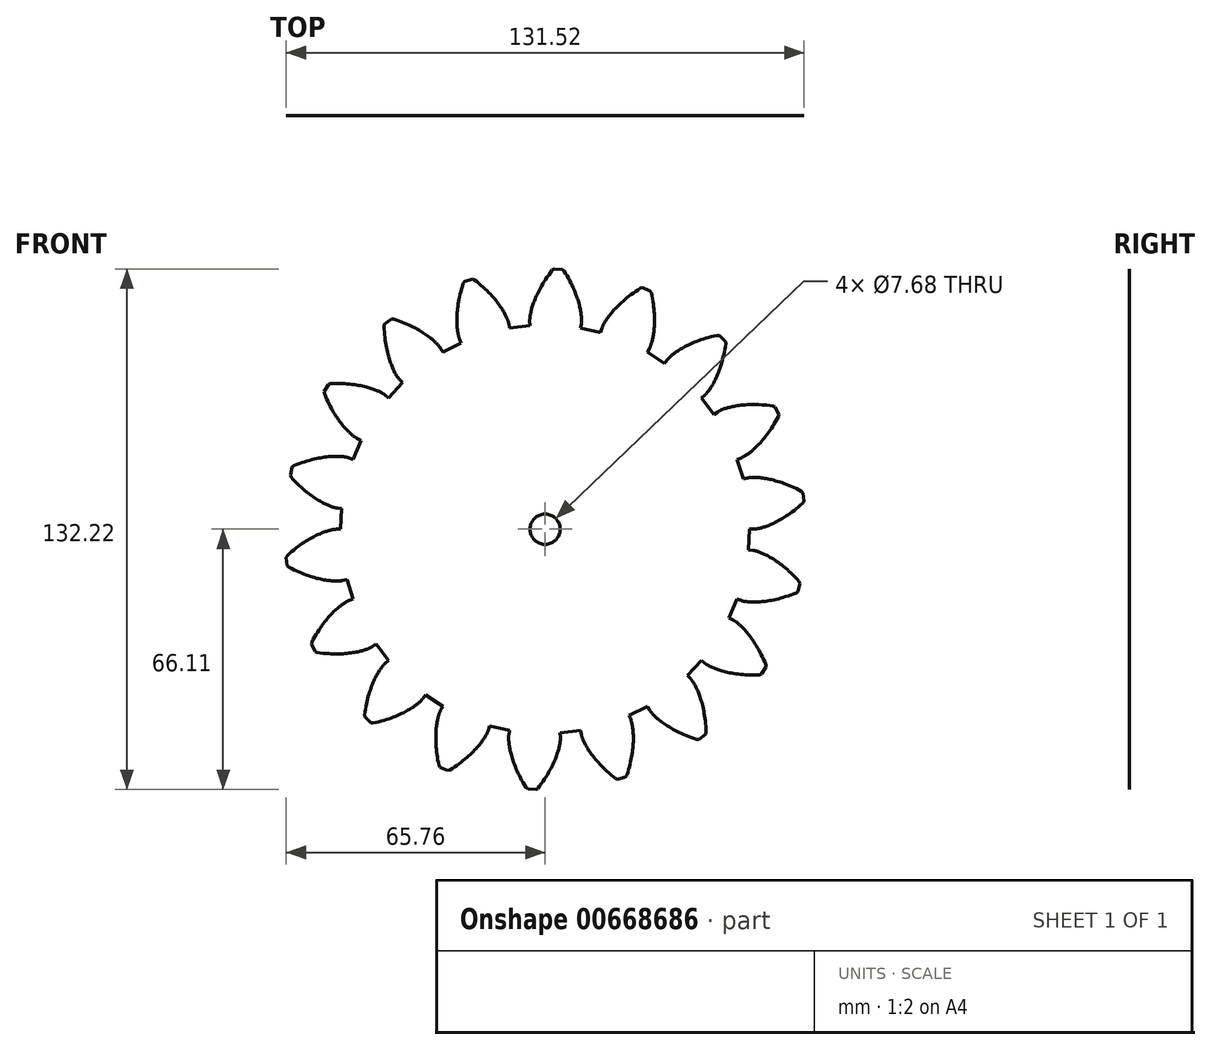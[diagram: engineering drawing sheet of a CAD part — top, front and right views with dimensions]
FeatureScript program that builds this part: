
annotation { "Feature Type Name" : "Feature", "Feature Type Description" : "" }
export const myFeature = defineFeature(function(context is Context, id is Id, definition is map)
    precondition{}
    {
        {
            var Q0;
            Q0=qCreatedBy(makeId("Front.planeOp"),FACE);
            var sketch = newSketch(context, id + "F0", { "sketchPlane" : qUnion([Q0])});
            skLineSegment(sketch, "E0", {"start": v(51.92, 0) * mm, "end": v(53.05, 0) * mm});
            skLineSegment(sketch, "E1", {"start": v(53.05, 0) * mm, "end": v(53.08, 0) * mm});
            skLineSegment(sketch, "E2", {"start": v(53.08, 0) * mm, "end": v(53.13, 0) * mm});
            skLineSegment(sketch, "E3", {"start": v(53.13, 0) * mm, "end": v(53.2, 0) * mm});
            skLineSegment(sketch, "E4", {"start": v(53.2, 0) * mm, "end": v(53.28, 0.01) * mm});
            skLineSegment(sketch, "E5", {"start": v(53.28, 0.01) * mm, "end": v(53.39, 0.03) * mm});
            skLineSegment(sketch, "E6", {"start": v(53.39, 0.03) * mm, "end": v(53.52, 0.04) * mm});
            skLineSegment(sketch, "E7", {"start": v(53.52, 0.04) * mm, "end": v(53.66, 0.06) * mm});
            skLineSegment(sketch, "E8", {"start": v(53.66, 0.06) * mm, "end": v(53.83, 0.1) * mm});
            skLineSegment(sketch, "E9", {"start": v(53.83, 0.1) * mm, "end": v(54.01, 0.12) * mm});
            skLineSegment(sketch, "E10", {"start": v(54.01, 0.12) * mm, "end": v(54.21, 0.17) * mm});
            skLineSegment(sketch, "E11", {"start": v(54.21, 0.17) * mm, "end": v(54.44, 0.22) * mm});
            skLineSegment(sketch, "E12", {"start": v(54.44, 0.22) * mm, "end": v(54.68, 0.28) * mm});
            skLineSegment(sketch, "E13", {"start": v(54.68, 0.28) * mm, "end": v(54.94, 0.34) * mm});
            skLineSegment(sketch, "E14", {"start": v(54.94, 0.34) * mm, "end": v(55.21, 0.42) * mm});
            skLineSegment(sketch, "E15", {"start": v(55.21, 0.42) * mm, "end": v(55.5, 0.51) * mm});
            skLineSegment(sketch, "E16", {"start": v(55.5, 0.51) * mm, "end": v(55.81, 0.62) * mm});
            skLineSegment(sketch, "E17", {"start": v(55.81, 0.62) * mm, "end": v(56.14, 0.73) * mm});
            skLineSegment(sketch, "E18", {"start": v(56.14, 0.73) * mm, "end": v(56.49, 0.86) * mm});
            skLineSegment(sketch, "E19", {"start": v(56.49, 0.86) * mm, "end": v(56.85, 1) * mm});
            skLineSegment(sketch, "E20", {"start": v(56.85, 1) * mm, "end": v(57.22, 1.16) * mm});
            skLineSegment(sketch, "E21", {"start": v(57.22, 1.16) * mm, "end": v(57.61, 1.33) * mm});
            skLineSegment(sketch, "E22", {"start": v(57.61, 1.33) * mm, "end": v(58.02, 1.52) * mm});
            skLineSegment(sketch, "E23", {"start": v(58.02, 1.52) * mm, "end": v(58.44, 1.72) * mm});
            skLineSegment(sketch, "E24", {"start": v(58.44, 1.72) * mm, "end": v(58.87, 1.94) * mm});
            skLineSegment(sketch, "E25", {"start": v(58.87, 1.94) * mm, "end": v(59.32, 2.18) * mm});
            skLineSegment(sketch, "E26", {"start": v(59.32, 2.18) * mm, "end": v(59.78, 2.44) * mm});
            skLineSegment(sketch, "E27", {"start": v(59.78, 2.44) * mm, "end": v(60.25, 2.72) * mm});
            skLineSegment(sketch, "E28", {"start": v(60.25, 2.72) * mm, "end": v(60.73, 3.01) * mm});
            skLineSegment(sketch, "E29", {"start": v(60.73, 3.01) * mm, "end": v(61.22, 3.33) * mm});
            skLineSegment(sketch, "E30", {"start": v(61.22, 3.33) * mm, "end": v(61.73, 3.67) * mm});
            skLineSegment(sketch, "E31", {"start": v(61.73, 3.67) * mm, "end": v(62.24, 4.03) * mm});
            skLineSegment(sketch, "E32", {"start": v(62.24, 4.03) * mm, "end": v(62.76, 4.4) * mm});
            skLineSegment(sketch, "E33", {"start": v(62.76, 4.4) * mm, "end": v(63.3, 4.8) * mm});
            skLineSegment(sketch, "E34", {"start": v(63.3, 4.8) * mm, "end": v(63.83, 5.23) * mm});
            skLineSegment(sketch, "E35", {"start": v(63.83, 5.23) * mm, "end": v(64.38, 5.68) * mm});
            skLineSegment(sketch, "E36", {"start": v(64.38, 5.68) * mm, "end": v(64.93, 6.15) * mm});
            skLineSegment(sketch, "E37", {"start": v(64.93, 6.15) * mm, "end": v(65.5, 6.65) * mm});
            skLineSegment(sketch, "E38", {"start": v(65.5, 6.65) * mm, "end": v(65.76, 7.14) * mm});
            skLineSegment(sketch, "E39", {"start": v(65.76, 7.14) * mm, "end": v(65.5, 9.23) * mm});
            skLineSegment(sketch, "E40", {"start": v(65.5, 9.23) * mm, "end": v(65.12, 9.64) * mm});
            skLineSegment(sketch, "E41", {"start": v(65.12, 9.64) * mm, "end": v(64.46, 9.98) * mm});
            skLineSegment(sketch, "E42", {"start": v(64.46, 9.98) * mm, "end": v(63.8, 10.3) * mm});
            skLineSegment(sketch, "E43", {"start": v(63.8, 10.3) * mm, "end": v(63.17, 10.6) * mm});
            skLineSegment(sketch, "E44", {"start": v(63.17, 10.6) * mm, "end": v(62.54, 10.88) * mm});
            skLineSegment(sketch, "E45", {"start": v(62.54, 10.88) * mm, "end": v(61.92, 11.14) * mm});
            skLineSegment(sketch, "E46", {"start": v(61.92, 11.14) * mm, "end": v(61.32, 11.38) * mm});
            skLineSegment(sketch, "E47", {"start": v(61.32, 11.38) * mm, "end": v(60.74, 11.6) * mm});
            skLineSegment(sketch, "E48", {"start": v(60.74, 11.6) * mm, "end": v(60.17, 11.8) * mm});
            skLineSegment(sketch, "E49", {"start": v(60.17, 11.8) * mm, "end": v(59.61, 12) * mm});
            skLineSegment(sketch, "E50", {"start": v(59.61, 12) * mm, "end": v(59.07, 12.16) * mm});
            skLineSegment(sketch, "E51", {"start": v(59.07, 12.16) * mm, "end": v(58.54, 12.31) * mm});
            skLineSegment(sketch, "E52", {"start": v(58.54, 12.31) * mm, "end": v(58.04, 12.45) * mm});
            skLineSegment(sketch, "E53", {"start": v(58.04, 12.45) * mm, "end": v(57.55, 12.57) * mm});
            skLineSegment(sketch, "E54", {"start": v(57.55, 12.57) * mm, "end": v(57.07, 12.68) * mm});
            skLineSegment(sketch, "E55", {"start": v(57.07, 12.68) * mm, "end": v(56.61, 12.78) * mm});
            skLineSegment(sketch, "E56", {"start": v(56.61, 12.78) * mm, "end": v(56.17, 12.86) * mm});
            skLineSegment(sketch, "E57", {"start": v(56.17, 12.86) * mm, "end": v(55.75, 12.93) * mm});
            skLineSegment(sketch, "E58", {"start": v(55.75, 12.93) * mm, "end": v(55.35, 13) * mm});
            skLineSegment(sketch, "E59", {"start": v(55.35, 13) * mm, "end": v(54.97, 13.04) * mm});
            skLineSegment(sketch, "E60", {"start": v(54.97, 13.04) * mm, "end": v(54.6, 13.08) * mm});
            skLineSegment(sketch, "E61", {"start": v(54.6, 13.08) * mm, "end": v(54.26, 13.11) * mm});
            skLineSegment(sketch, "E62", {"start": v(54.26, 13.11) * mm, "end": v(53.93, 13.13) * mm});
            skLineSegment(sketch, "E63", {"start": v(53.93, 13.13) * mm, "end": v(53.62, 13.15) * mm});
            skLineSegment(sketch, "E64", {"start": v(53.62, 13.15) * mm, "end": v(53.34, 13.16) * mm});
            skLineSegment(sketch, "E65", {"start": v(53.34, 13.16) * mm, "end": v(53.07, 13.16) * mm});
            skLineSegment(sketch, "E66", {"start": v(53.07, 13.16) * mm, "end": v(52.82, 13.16) * mm});
            skLineSegment(sketch, "E67", {"start": v(52.82, 13.16) * mm, "end": v(52.6, 13.15) * mm});
            skLineSegment(sketch, "E68", {"start": v(52.6, 13.15) * mm, "end": v(52.39, 13.15) * mm});
            skLineSegment(sketch, "E69", {"start": v(52.39, 13.15) * mm, "end": v(52.2, 13.13) * mm});
            skLineSegment(sketch, "E70", {"start": v(52.2, 13.13) * mm, "end": v(52.03, 13.12) * mm});
            skLineSegment(sketch, "E71", {"start": v(52.03, 13.12) * mm, "end": v(51.89, 13.1) * mm});
            skLineSegment(sketch, "E72", {"start": v(51.89, 13.1) * mm, "end": v(51.76, 13.09) * mm});
            skLineSegment(sketch, "E73", {"start": v(51.76, 13.09) * mm, "end": v(51.65, 13.07) * mm});
            skLineSegment(sketch, "E74", {"start": v(51.65, 13.07) * mm, "end": v(51.57, 13.06) * mm});
            skLineSegment(sketch, "E75", {"start": v(51.57, 13.06) * mm, "end": v(51.5, 13.05) * mm});
            skLineSegment(sketch, "E76", {"start": v(51.5, 13.05) * mm, "end": v(51.45, 13.04) * mm});
            skLineSegment(sketch, "E77", {"start": v(51.45, 13.04) * mm, "end": v(51.43, 13.03) * mm});
            skLineSegment(sketch, "E78", {"start": v(51.43, 13.03) * mm, "end": v(50.33, 12.75) * mm});
            skLineSegment(sketch, "E79", {"start": v(50.33, 12.75) * mm, "end": v(48.8, 17.76) * mm});
            skLineSegment(sketch, "E80", {"start": v(48.8, 17.76) * mm, "end": v(49.85, 18.14) * mm});
            skLineSegment(sketch, "E81", {"start": v(49.85, 18.14) * mm, "end": v(49.88, 18.15) * mm});
            skLineSegment(sketch, "E82", {"start": v(49.88, 18.15) * mm, "end": v(49.92, 18.17) * mm});
            skLineSegment(sketch, "E83", {"start": v(49.92, 18.17) * mm, "end": v(49.98, 18.2) * mm});
            skLineSegment(sketch, "E84", {"start": v(49.98, 18.2) * mm, "end": v(50.06, 18.24) * mm});
            skLineSegment(sketch, "E85", {"start": v(50.06, 18.24) * mm, "end": v(50.16, 18.29) * mm});
            skLineSegment(sketch, "E86", {"start": v(50.16, 18.29) * mm, "end": v(50.27, 18.34) * mm});
            skLineSegment(sketch, "E87", {"start": v(50.27, 18.34) * mm, "end": v(50.4, 18.41) * mm});
            skLineSegment(sketch, "E88", {"start": v(50.4, 18.41) * mm, "end": v(50.55, 18.5) * mm});
            skLineSegment(sketch, "E89", {"start": v(50.55, 18.5) * mm, "end": v(50.71, 18.59) * mm});
            skLineSegment(sketch, "E90", {"start": v(50.71, 18.59) * mm, "end": v(50.89, 18.7) * mm});
            skLineSegment(sketch, "E91", {"start": v(50.89, 18.7) * mm, "end": v(51.08, 18.82) * mm});
            skLineSegment(sketch, "E92", {"start": v(51.08, 18.82) * mm, "end": v(51.29, 18.96) * mm});
            skLineSegment(sketch, "E93", {"start": v(51.29, 18.96) * mm, "end": v(51.5, 19.11) * mm});
            skLineSegment(sketch, "E94", {"start": v(51.5, 19.11) * mm, "end": v(51.74, 19.28) * mm});
            skLineSegment(sketch, "E95", {"start": v(51.74, 19.28) * mm, "end": v(51.98, 19.47) * mm});
            skLineSegment(sketch, "E96", {"start": v(51.98, 19.47) * mm, "end": v(52.24, 19.67) * mm});
            skLineSegment(sketch, "E97", {"start": v(52.24, 19.67) * mm, "end": v(52.5, 19.89) * mm});
            skLineSegment(sketch, "E98", {"start": v(52.5, 19.89) * mm, "end": v(52.79, 20.13) * mm});
            skLineSegment(sketch, "E99", {"start": v(52.79, 20.13) * mm, "end": v(53.08, 20.38) * mm});
            skLineSegment(sketch, "E100", {"start": v(53.08, 20.38) * mm, "end": v(53.38, 20.66) * mm});
            skLineSegment(sketch, "E101", {"start": v(53.38, 20.66) * mm, "end": v(53.68, 20.95) * mm});
            skLineSegment(sketch, "E102", {"start": v(53.68, 20.95) * mm, "end": v(54, 21.27) * mm});
            skLineSegment(sketch, "E103", {"start": v(54, 21.27) * mm, "end": v(54.32, 21.6) * mm});
            skLineSegment(sketch, "E104", {"start": v(54.32, 21.6) * mm, "end": v(54.66, 21.96) * mm});
            skLineSegment(sketch, "E105", {"start": v(54.66, 21.96) * mm, "end": v(55, 22.34) * mm});
            skLineSegment(sketch, "E106", {"start": v(55, 22.34) * mm, "end": v(55.34, 22.74) * mm});
            skLineSegment(sketch, "E107", {"start": v(55.34, 22.74) * mm, "end": v(55.68, 23.16) * mm});
            skLineSegment(sketch, "E108", {"start": v(55.68, 23.16) * mm, "end": v(56.04, 23.6) * mm});
            skLineSegment(sketch, "E109", {"start": v(56.04, 23.6) * mm, "end": v(56.4, 24.07) * mm});
            skLineSegment(sketch, "E110", {"start": v(56.4, 24.07) * mm, "end": v(56.75, 24.56) * mm});
            skLineSegment(sketch, "E111", {"start": v(56.75, 24.56) * mm, "end": v(57.11, 25.07) * mm});
            skLineSegment(sketch, "E112", {"start": v(57.11, 25.07) * mm, "end": v(57.47, 25.6) * mm});
            skLineSegment(sketch, "E113", {"start": v(57.47, 25.6) * mm, "end": v(57.83, 26.17) * mm});
            skLineSegment(sketch, "E114", {"start": v(57.83, 26.17) * mm, "end": v(58.2, 26.75) * mm});
            skLineSegment(sketch, "E115", {"start": v(58.2, 26.75) * mm, "end": v(58.56, 27.36) * mm});
            skLineSegment(sketch, "E116", {"start": v(58.56, 27.36) * mm, "end": v(58.91, 28) * mm});
            skLineSegment(sketch, "E117", {"start": v(58.91, 28) * mm, "end": v(59.27, 28.65) * mm});
            skLineSegment(sketch, "E118", {"start": v(59.27, 28.65) * mm, "end": v(59.35, 29.2) * mm});
            skLineSegment(sketch, "E119", {"start": v(59.35, 29.2) * mm, "end": v(58.39, 31.08) * mm});
            skLineSegment(sketch, "E120", {"start": v(58.39, 31.08) * mm, "end": v(57.9, 31.33) * mm});
            skLineSegment(sketch, "E121", {"start": v(57.9, 31.33) * mm, "end": v(57.15, 31.43) * mm});
            skLineSegment(sketch, "E122", {"start": v(57.15, 31.43) * mm, "end": v(56.43, 31.5) * mm});
            skLineSegment(sketch, "E123", {"start": v(56.43, 31.5) * mm, "end": v(55.73, 31.57) * mm});
            skLineSegment(sketch, "E124", {"start": v(55.73, 31.57) * mm, "end": v(55.04, 31.62) * mm});
            skLineSegment(sketch, "E125", {"start": v(55.04, 31.62) * mm, "end": v(54.38, 31.65) * mm});
            skLineSegment(sketch, "E126", {"start": v(54.38, 31.65) * mm, "end": v(53.73, 31.67) * mm});
            skLineSegment(sketch, "E127", {"start": v(53.73, 31.67) * mm, "end": v(53.1, 31.68) * mm});
            skLineSegment(sketch, "E128", {"start": v(53.1, 31.68) * mm, "end": v(52.5, 31.67) * mm});
            skLineSegment(sketch, "E129", {"start": v(52.5, 31.67) * mm, "end": v(51.91, 31.66) * mm});
            skLineSegment(sketch, "E130", {"start": v(51.91, 31.66) * mm, "end": v(51.35, 31.63) * mm});
            skLineSegment(sketch, "E131", {"start": v(51.35, 31.63) * mm, "end": v(50.8, 31.6) * mm});
            skLineSegment(sketch, "E132", {"start": v(50.8, 31.6) * mm, "end": v(50.28, 31.55) * mm});
            skLineSegment(sketch, "E133", {"start": v(50.28, 31.55) * mm, "end": v(49.77, 31.5) * mm});
            skLineSegment(sketch, "E134", {"start": v(49.77, 31.5) * mm, "end": v(49.3, 31.44) * mm});
            skLineSegment(sketch, "E135", {"start": v(49.3, 31.44) * mm, "end": v(48.83, 31.37) * mm});
            skLineSegment(sketch, "E136", {"start": v(48.83, 31.37) * mm, "end": v(48.39, 31.3) * mm});
            skLineSegment(sketch, "E137", {"start": v(48.39, 31.3) * mm, "end": v(47.97, 31.22) * mm});
            skLineSegment(sketch, "E138", {"start": v(47.97, 31.22) * mm, "end": v(47.57, 31.14) * mm});
            skLineSegment(sketch, "E139", {"start": v(47.57, 31.14) * mm, "end": v(47.2, 31.05) * mm});
            skLineSegment(sketch, "E140", {"start": v(47.2, 31.05) * mm, "end": v(46.84, 30.97) * mm});
            skLineSegment(sketch, "E141", {"start": v(46.84, 30.97) * mm, "end": v(46.5, 30.88) * mm});
            skLineSegment(sketch, "E142", {"start": v(46.5, 30.88) * mm, "end": v(46.19, 30.79) * mm});
            skLineSegment(sketch, "E143", {"start": v(46.19, 30.79) * mm, "end": v(45.9, 30.7) * mm});
            skLineSegment(sketch, "E144", {"start": v(45.9, 30.7) * mm, "end": v(45.62, 30.6) * mm});
            skLineSegment(sketch, "E145", {"start": v(45.62, 30.6) * mm, "end": v(45.37, 30.52) * mm});
            skLineSegment(sketch, "E146", {"start": v(45.37, 30.52) * mm, "end": v(45.13, 30.43) * mm});
            skLineSegment(sketch, "E147", {"start": v(45.13, 30.43) * mm, "end": v(44.92, 30.35) * mm});
            skLineSegment(sketch, "E148", {"start": v(44.92, 30.35) * mm, "end": v(44.73, 30.27) * mm});
            skLineSegment(sketch, "E149", {"start": v(44.73, 30.27) * mm, "end": v(44.56, 30.2) * mm});
            skLineSegment(sketch, "E150", {"start": v(44.56, 30.2) * mm, "end": v(44.4, 30.12) * mm});
            skLineSegment(sketch, "E151", {"start": v(44.4, 30.12) * mm, "end": v(44.28, 30.06) * mm});
            skLineSegment(sketch, "E152", {"start": v(44.28, 30.06) * mm, "end": v(44.16, 30) * mm});
            skLineSegment(sketch, "E153", {"start": v(44.16, 30) * mm, "end": v(44.07, 29.95) * mm});
            skLineSegment(sketch, "E154", {"start": v(44.07, 29.95) * mm, "end": v(44, 29.9) * mm});
            skLineSegment(sketch, "E155", {"start": v(44, 29.9) * mm, "end": v(43.93, 29.87) * mm});
            skLineSegment(sketch, "E156", {"start": v(43.93, 29.87) * mm, "end": v(43.9, 29.85) * mm});
            skLineSegment(sketch, "E157", {"start": v(43.9, 29.85) * mm, "end": v(43.87, 29.83) * mm});
            skLineSegment(sketch, "E158", {"start": v(43.87, 29.83) * mm, "end": v(42.94, 29.2) * mm});
            skLineSegment(sketch, "E159", {"start": v(42.94, 29.2) * mm, "end": v(39.78, 33.38) * mm});
            skLineSegment(sketch, "E160", {"start": v(39.78, 33.38) * mm, "end": v(40.64, 34.1) * mm});
            skLineSegment(sketch, "E161", {"start": v(40.64, 34.1) * mm, "end": v(40.66, 34.12) * mm});
            skLineSegment(sketch, "E162", {"start": v(40.66, 34.12) * mm, "end": v(40.7, 34.15) * mm});
            skLineSegment(sketch, "E163", {"start": v(40.7, 34.15) * mm, "end": v(40.74, 34.2) * mm});
            skLineSegment(sketch, "E164", {"start": v(40.74, 34.2) * mm, "end": v(40.8, 34.26) * mm});
            skLineSegment(sketch, "E165", {"start": v(40.8, 34.26) * mm, "end": v(40.88, 34.34) * mm});
            skLineSegment(sketch, "E166", {"start": v(40.88, 34.34) * mm, "end": v(40.97, 34.43) * mm});
            skLineSegment(sketch, "E167", {"start": v(40.97, 34.43) * mm, "end": v(41.07, 34.54) * mm});
            skLineSegment(sketch, "E168", {"start": v(41.07, 34.54) * mm, "end": v(41.18, 34.67) * mm});
            skLineSegment(sketch, "E169", {"start": v(41.18, 34.67) * mm, "end": v(41.3, 34.81) * mm});
            skLineSegment(sketch, "E170", {"start": v(41.3, 34.81) * mm, "end": v(41.42, 34.98) * mm});
            skLineSegment(sketch, "E171", {"start": v(41.42, 34.98) * mm, "end": v(41.56, 35.16) * mm});
            skLineSegment(sketch, "E172", {"start": v(41.56, 35.16) * mm, "end": v(41.7, 35.36) * mm});
            skLineSegment(sketch, "E173", {"start": v(41.7, 35.36) * mm, "end": v(41.86, 35.58) * mm});
            skLineSegment(sketch, "E174", {"start": v(41.86, 35.58) * mm, "end": v(42.02, 35.81) * mm});
            skLineSegment(sketch, "E175", {"start": v(42.02, 35.81) * mm, "end": v(42.19, 36.07) * mm});
            skLineSegment(sketch, "E176", {"start": v(42.19, 36.07) * mm, "end": v(42.36, 36.35) * mm});
            skLineSegment(sketch, "E177", {"start": v(42.36, 36.35) * mm, "end": v(42.54, 36.65) * mm});
            skLineSegment(sketch, "E178", {"start": v(42.54, 36.65) * mm, "end": v(42.72, 36.97) * mm});
            skLineSegment(sketch, "E179", {"start": v(42.72, 36.97) * mm, "end": v(42.9, 37.3) * mm});
            skLineSegment(sketch, "E180", {"start": v(42.9, 37.3) * mm, "end": v(43.09, 37.67) * mm});
            skLineSegment(sketch, "E181", {"start": v(43.09, 37.67) * mm, "end": v(43.28, 38.05) * mm});
            skLineSegment(sketch, "E182", {"start": v(43.28, 38.05) * mm, "end": v(43.47, 38.46) * mm});
            skLineSegment(sketch, "E183", {"start": v(43.47, 38.46) * mm, "end": v(43.66, 38.88) * mm});
            skLineSegment(sketch, "E184", {"start": v(43.66, 38.88) * mm, "end": v(43.85, 39.33) * mm});
            skLineSegment(sketch, "E185", {"start": v(43.85, 39.33) * mm, "end": v(44.04, 39.8) * mm});
            skLineSegment(sketch, "E186", {"start": v(44.04, 39.8) * mm, "end": v(44.22, 40.3) * mm});
            skLineSegment(sketch, "E187", {"start": v(44.22, 40.3) * mm, "end": v(44.4, 40.8) * mm});
            skLineSegment(sketch, "E188", {"start": v(44.4, 40.8) * mm, "end": v(44.58, 41.35) * mm});
            skLineSegment(sketch, "E189", {"start": v(44.58, 41.35) * mm, "end": v(44.76, 41.9) * mm});
            skLineSegment(sketch, "E190", {"start": v(44.76, 41.9) * mm, "end": v(44.93, 42.49) * mm});
            skLineSegment(sketch, "E191", {"start": v(44.93, 42.49) * mm, "end": v(45.1, 43.1) * mm});
            skLineSegment(sketch, "E192", {"start": v(45.1, 43.1) * mm, "end": v(45.25, 43.72) * mm});
            skLineSegment(sketch, "E193", {"start": v(45.25, 43.72) * mm, "end": v(45.4, 44.37) * mm});
            skLineSegment(sketch, "E194", {"start": v(45.4, 44.37) * mm, "end": v(45.54, 45.04) * mm});
            skLineSegment(sketch, "E195", {"start": v(45.54, 45.04) * mm, "end": v(45.67, 45.74) * mm});
            skLineSegment(sketch, "E196", {"start": v(45.67, 45.74) * mm, "end": v(45.79, 46.45) * mm});
            skLineSegment(sketch, "E197", {"start": v(45.79, 46.45) * mm, "end": v(45.9, 47.19) * mm});
            skLineSegment(sketch, "E198", {"start": v(45.9, 47.19) * mm, "end": v(45.79, 47.74) * mm});
            skLineSegment(sketch, "E199", {"start": v(45.79, 47.74) * mm, "end": v(44.24, 49.18) * mm});
            skLineSegment(sketch, "E200", {"start": v(44.24, 49.18) * mm, "end": v(43.69, 49.24) * mm});
            skLineSegment(sketch, "E201", {"start": v(43.69, 49.24) * mm, "end": v(42.96, 49.08) * mm});
            skLineSegment(sketch, "E202", {"start": v(42.96, 49.08) * mm, "end": v(42.25, 48.9) * mm});
            skLineSegment(sketch, "E203", {"start": v(42.25, 48.9) * mm, "end": v(41.57, 48.72) * mm});
            skLineSegment(sketch, "E204", {"start": v(41.57, 48.72) * mm, "end": v(40.91, 48.54) * mm});
            skLineSegment(sketch, "E205", {"start": v(40.91, 48.54) * mm, "end": v(40.27, 48.34) * mm});
            skLineSegment(sketch, "E206", {"start": v(40.27, 48.34) * mm, "end": v(39.66, 48.14) * mm});
            skLineSegment(sketch, "E207", {"start": v(39.66, 48.14) * mm, "end": v(39.07, 47.93) * mm});
            skLineSegment(sketch, "E208", {"start": v(39.07, 47.93) * mm, "end": v(38.5, 47.72) * mm});
            skLineSegment(sketch, "E209", {"start": v(38.5, 47.72) * mm, "end": v(37.96, 47.5) * mm});
            skLineSegment(sketch, "E210", {"start": v(37.96, 47.5) * mm, "end": v(37.43, 47.29) * mm});
            skLineSegment(sketch, "E211", {"start": v(37.43, 47.29) * mm, "end": v(36.93, 47.07) * mm});
            skLineSegment(sketch, "E212", {"start": v(36.93, 47.07) * mm, "end": v(36.45, 46.84) * mm});
            skLineSegment(sketch, "E213", {"start": v(36.45, 46.84) * mm, "end": v(36, 46.62) * mm});
            skLineSegment(sketch, "E214", {"start": v(36, 46.62) * mm, "end": v(35.57, 46.4) * mm});
            skLineSegment(sketch, "E215", {"start": v(35.57, 46.4) * mm, "end": v(35.15, 46.18) * mm});
            skLineSegment(sketch, "E216", {"start": v(35.15, 46.18) * mm, "end": v(34.77, 45.96) * mm});
            skLineSegment(sketch, "E217", {"start": v(34.77, 45.96) * mm, "end": v(34.4, 45.74) * mm});
            skLineSegment(sketch, "E218", {"start": v(34.4, 45.74) * mm, "end": v(34.05, 45.53) * mm});
            skLineSegment(sketch, "E219", {"start": v(34.05, 45.53) * mm, "end": v(33.72, 45.32) * mm});
            skLineSegment(sketch, "E220", {"start": v(33.72, 45.32) * mm, "end": v(33.42, 45.12) * mm});
            skLineSegment(sketch, "E221", {"start": v(33.42, 45.12) * mm, "end": v(33.13, 44.92) * mm});
            skLineSegment(sketch, "E222", {"start": v(33.13, 44.92) * mm, "end": v(32.87, 44.73) * mm});
            skLineSegment(sketch, "E223", {"start": v(32.87, 44.73) * mm, "end": v(32.62, 44.54) * mm});
            skLineSegment(sketch, "E224", {"start": v(32.62, 44.54) * mm, "end": v(32.4, 44.36) * mm});
            skLineSegment(sketch, "E225", {"start": v(32.4, 44.36) * mm, "end": v(32.2, 44.2) * mm});
            skLineSegment(sketch, "E226", {"start": v(32.2, 44.2) * mm, "end": v(32, 44.03) * mm});
            skLineSegment(sketch, "E227", {"start": v(32, 44.03) * mm, "end": v(31.83, 43.88) * mm});
            skLineSegment(sketch, "E228", {"start": v(31.83, 43.88) * mm, "end": v(31.68, 43.74) * mm});
            skLineSegment(sketch, "E229", {"start": v(31.68, 43.74) * mm, "end": v(31.55, 43.61) * mm});
            skLineSegment(sketch, "E230", {"start": v(31.55, 43.61) * mm, "end": v(31.43, 43.5) * mm});
            skLineSegment(sketch, "E231", {"start": v(31.43, 43.5) * mm, "end": v(31.33, 43.39) * mm});
            skLineSegment(sketch, "E232", {"start": v(31.33, 43.39) * mm, "end": v(31.24, 43.3) * mm});
            skLineSegment(sketch, "E233", {"start": v(31.24, 43.3) * mm, "end": v(31.17, 43.22) * mm});
            skLineSegment(sketch, "E234", {"start": v(31.17, 43.22) * mm, "end": v(31.1, 43.15) * mm});
            skLineSegment(sketch, "E235", {"start": v(31.1, 43.15) * mm, "end": v(31.07, 43.1) * mm});
            skLineSegment(sketch, "E236", {"start": v(31.07, 43.1) * mm, "end": v(31.04, 43.06) * mm});
            skLineSegment(sketch, "E237", {"start": v(31.04, 43.06) * mm, "end": v(31.02, 43.04) * mm});
            skLineSegment(sketch, "E238", {"start": v(31.02, 43.04) * mm, "end": v(30.36, 42.12) * mm});
            skLineSegment(sketch, "E239", {"start": v(30.36, 42.12) * mm, "end": v(25.96, 44.97) * mm});
            skLineSegment(sketch, "E240", {"start": v(25.96, 44.97) * mm, "end": v(26.53, 45.94) * mm});
            skLineSegment(sketch, "E241", {"start": v(26.53, 45.94) * mm, "end": v(26.54, 45.97) * mm});
            skLineSegment(sketch, "E242", {"start": v(26.54, 45.97) * mm, "end": v(26.56, 46) * mm});
            skLineSegment(sketch, "E243", {"start": v(26.56, 46) * mm, "end": v(26.6, 46.07) * mm});
            skLineSegment(sketch, "E244", {"start": v(26.6, 46.07) * mm, "end": v(26.63, 46.15) * mm});
            skLineSegment(sketch, "E245", {"start": v(26.63, 46.15) * mm, "end": v(26.67, 46.25) * mm});
            skLineSegment(sketch, "E246", {"start": v(26.67, 46.25) * mm, "end": v(26.72, 46.37) * mm});
            skLineSegment(sketch, "E247", {"start": v(26.72, 46.37) * mm, "end": v(26.78, 46.5) * mm});
            skLineSegment(sketch, "E248", {"start": v(26.78, 46.5) * mm, "end": v(26.83, 46.66) * mm});
            skLineSegment(sketch, "E249", {"start": v(26.83, 46.66) * mm, "end": v(26.9, 46.84) * mm});
            skLineSegment(sketch, "E250", {"start": v(26.9, 46.84) * mm, "end": v(26.96, 47.03) * mm});
            skLineSegment(sketch, "E251", {"start": v(26.96, 47.03) * mm, "end": v(27.03, 47.25) * mm});
            skLineSegment(sketch, "E252", {"start": v(27.03, 47.25) * mm, "end": v(27.1, 47.49) * mm});
            skLineSegment(sketch, "E253", {"start": v(27.1, 47.49) * mm, "end": v(27.17, 47.75) * mm});
            skLineSegment(sketch, "E254", {"start": v(27.17, 47.75) * mm, "end": v(27.24, 48.03) * mm});
            skLineSegment(sketch, "E255", {"start": v(27.24, 48.03) * mm, "end": v(27.3, 48.32) * mm});
            skLineSegment(sketch, "E256", {"start": v(27.3, 48.32) * mm, "end": v(27.37, 48.64) * mm});
            skLineSegment(sketch, "E257", {"start": v(27.37, 48.64) * mm, "end": v(27.44, 48.99) * mm});
            skLineSegment(sketch, "E258", {"start": v(27.44, 48.99) * mm, "end": v(27.5, 49.35) * mm});
            skLineSegment(sketch, "E259", {"start": v(27.5, 49.35) * mm, "end": v(27.56, 49.73) * mm});
            skLineSegment(sketch, "E260", {"start": v(27.56, 49.73) * mm, "end": v(27.6, 50.13) * mm});
            skLineSegment(sketch, "E261", {"start": v(27.6, 50.13) * mm, "end": v(27.65, 50.56) * mm});
            skLineSegment(sketch, "E262", {"start": v(27.65, 50.56) * mm, "end": v(27.7, 51) * mm});
            skLineSegment(sketch, "E263", {"start": v(27.7, 51) * mm, "end": v(27.73, 51.47) * mm});
            skLineSegment(sketch, "E264", {"start": v(27.73, 51.47) * mm, "end": v(27.75, 51.96) * mm});
            skLineSegment(sketch, "E265", {"start": v(27.75, 51.96) * mm, "end": v(27.77, 52.46) * mm});
            skLineSegment(sketch, "E266", {"start": v(27.77, 52.46) * mm, "end": v(27.77, 52.99) * mm});
            skLineSegment(sketch, "E267", {"start": v(27.77, 52.99) * mm, "end": v(27.77, 53.54) * mm});
            skLineSegment(sketch, "E268", {"start": v(27.77, 53.54) * mm, "end": v(27.75, 54.1) * mm});
            skLineSegment(sketch, "E269", {"start": v(27.75, 54.1) * mm, "end": v(27.73, 54.69) * mm});
            skLineSegment(sketch, "E270", {"start": v(27.73, 54.69) * mm, "end": v(27.69, 55.3) * mm});
            skLineSegment(sketch, "E271", {"start": v(27.69, 55.3) * mm, "end": v(27.63, 55.92) * mm});
            skLineSegment(sketch, "E272", {"start": v(27.63, 55.92) * mm, "end": v(27.56, 56.56) * mm});
            skLineSegment(sketch, "E273", {"start": v(27.56, 56.56) * mm, "end": v(27.48, 57.22) * mm});
            skLineSegment(sketch, "E274", {"start": v(27.48, 57.22) * mm, "end": v(27.38, 57.9) * mm});
            skLineSegment(sketch, "E275", {"start": v(27.38, 57.9) * mm, "end": v(27.27, 58.6) * mm});
            skLineSegment(sketch, "E276", {"start": v(27.27, 58.6) * mm, "end": v(27.14, 59.31) * mm});
            skLineSegment(sketch, "E277", {"start": v(27.14, 59.31) * mm, "end": v(26.99, 60.04) * mm});
            skLineSegment(sketch, "E278", {"start": v(26.99, 60.04) * mm, "end": v(26.7, 60.52) * mm});
            skLineSegment(sketch, "E279", {"start": v(26.7, 60.52) * mm, "end": v(24.75, 61.34) * mm});
            skLineSegment(sketch, "E280", {"start": v(24.75, 61.34) * mm, "end": v(24.2, 61.22) * mm});
            skLineSegment(sketch, "E281", {"start": v(24.2, 61.22) * mm, "end": v(23.58, 60.81) * mm});
            skLineSegment(sketch, "E282", {"start": v(23.58, 60.81) * mm, "end": v(22.98, 60.4) * mm});
            skLineSegment(sketch, "E283", {"start": v(22.98, 60.4) * mm, "end": v(22.4, 60) * mm});
            skLineSegment(sketch, "E284", {"start": v(22.4, 60) * mm, "end": v(21.84, 59.6) * mm});
            skLineSegment(sketch, "E285", {"start": v(21.84, 59.6) * mm, "end": v(21.31, 59.2) * mm});
            skLineSegment(sketch, "E286", {"start": v(21.31, 59.2) * mm, "end": v(20.8, 58.8) * mm});
            skLineSegment(sketch, "E287", {"start": v(20.8, 58.8) * mm, "end": v(20.32, 58.4) * mm});
            skLineSegment(sketch, "E288", {"start": v(20.32, 58.4) * mm, "end": v(19.86, 58.01) * mm});
            skLineSegment(sketch, "E289", {"start": v(19.86, 58.01) * mm, "end": v(19.42, 57.62) * mm});
            skLineSegment(sketch, "E290", {"start": v(19.42, 57.62) * mm, "end": v(19, 57.24) * mm});
            skLineSegment(sketch, "E291", {"start": v(19, 57.24) * mm, "end": v(18.6, 56.86) * mm});
            skLineSegment(sketch, "E292", {"start": v(18.6, 56.86) * mm, "end": v(18.24, 56.49) * mm});
            skLineSegment(sketch, "E293", {"start": v(18.24, 56.49) * mm, "end": v(17.88, 56.12) * mm});
            skLineSegment(sketch, "E294", {"start": v(17.88, 56.12) * mm, "end": v(17.55, 55.77) * mm});
            skLineSegment(sketch, "E295", {"start": v(17.55, 55.77) * mm, "end": v(17.24, 55.42) * mm});
            skLineSegment(sketch, "E296", {"start": v(17.24, 55.42) * mm, "end": v(16.95, 55.08) * mm});
            skLineSegment(sketch, "E297", {"start": v(16.95, 55.08) * mm, "end": v(16.68, 54.75) * mm});
            skLineSegment(sketch, "E298", {"start": v(16.68, 54.75) * mm, "end": v(16.43, 54.43) * mm});
            skLineSegment(sketch, "E299", {"start": v(16.43, 54.43) * mm, "end": v(16.19, 54.12) * mm});
            skLineSegment(sketch, "E300", {"start": v(16.19, 54.12) * mm, "end": v(15.97, 53.83) * mm});
            skLineSegment(sketch, "E301", {"start": v(15.97, 53.83) * mm, "end": v(15.77, 53.54) * mm});
            skLineSegment(sketch, "E302", {"start": v(15.77, 53.54) * mm, "end": v(15.59, 53.27) * mm});
            skLineSegment(sketch, "E303", {"start": v(15.59, 53.27) * mm, "end": v(15.42, 53.01) * mm});
            skLineSegment(sketch, "E304", {"start": v(15.42, 53.01) * mm, "end": v(15.27, 52.77) * mm});
            skLineSegment(sketch, "E305", {"start": v(15.27, 52.77) * mm, "end": v(15.14, 52.54) * mm});
            skLineSegment(sketch, "E306", {"start": v(15.14, 52.54) * mm, "end": v(15.01, 52.33) * mm});
            skLineSegment(sketch, "E307", {"start": v(15.01, 52.33) * mm, "end": v(14.9, 52.13) * mm});
            skLineSegment(sketch, "E308", {"start": v(14.9, 52.13) * mm, "end": v(14.8, 51.94) * mm});
            skLineSegment(sketch, "E309", {"start": v(14.8, 51.94) * mm, "end": v(14.73, 51.77) * mm});
            skLineSegment(sketch, "E310", {"start": v(14.73, 51.77) * mm, "end": v(14.66, 51.62) * mm});
            skLineSegment(sketch, "E311", {"start": v(14.66, 51.62) * mm, "end": v(14.6, 51.49) * mm});
            skLineSegment(sketch, "E312", {"start": v(14.6, 51.49) * mm, "end": v(14.55, 51.37) * mm});
            skLineSegment(sketch, "E313", {"start": v(14.55, 51.37) * mm, "end": v(14.5, 51.27) * mm});
            skLineSegment(sketch, "E314", {"start": v(14.5, 51.27) * mm, "end": v(14.47, 51.19) * mm});
            skLineSegment(sketch, "E315", {"start": v(14.47, 51.19) * mm, "end": v(14.45, 51.12) * mm});
            skLineSegment(sketch, "E316", {"start": v(14.45, 51.12) * mm, "end": v(14.44, 51.08) * mm});
            skLineSegment(sketch, "E317", {"start": v(14.44, 51.08) * mm, "end": v(14.43, 51.05) * mm});
            skLineSegment(sketch, "E318", {"start": v(14.43, 51.05) * mm, "end": v(14.12, 49.97) * mm});
            skLineSegment(sketch, "E319", {"start": v(14.12, 49.97) * mm, "end": v(9.02, 51.14) * mm});
            skLineSegment(sketch, "E320", {"start": v(9.02, 51.14) * mm, "end": v(9.21, 52.24) * mm});
            skLineSegment(sketch, "E321", {"start": v(9.21, 52.24) * mm, "end": v(9.22, 52.27) * mm});
            skLineSegment(sketch, "E322", {"start": v(9.22, 52.27) * mm, "end": v(9.22, 52.32) * mm});
            skLineSegment(sketch, "E323", {"start": v(9.22, 52.32) * mm, "end": v(9.23, 52.39) * mm});
            skLineSegment(sketch, "E324", {"start": v(9.23, 52.39) * mm, "end": v(9.24, 52.47) * mm});
            skLineSegment(sketch, "E325", {"start": v(9.24, 52.47) * mm, "end": v(9.25, 52.58) * mm});
            skLineSegment(sketch, "E326", {"start": v(9.25, 52.58) * mm, "end": v(9.25, 52.7) * mm});
            skLineSegment(sketch, "E327", {"start": v(9.25, 52.7) * mm, "end": v(9.26, 52.86) * mm});
            skLineSegment(sketch, "E328", {"start": v(9.26, 52.86) * mm, "end": v(9.26, 53.03) * mm});
            skLineSegment(sketch, "E329", {"start": v(9.26, 53.03) * mm, "end": v(9.26, 53.21) * mm});
            skLineSegment(sketch, "E330", {"start": v(9.26, 53.21) * mm, "end": v(9.25, 53.42) * mm});
            skLineSegment(sketch, "E331", {"start": v(9.25, 53.42) * mm, "end": v(9.24, 53.65) * mm});
            skLineSegment(sketch, "E332", {"start": v(9.24, 53.65) * mm, "end": v(9.22, 53.9) * mm});
            skLineSegment(sketch, "E333", {"start": v(9.22, 53.9) * mm, "end": v(9.2, 54.16) * mm});
            skLineSegment(sketch, "E334", {"start": v(9.2, 54.16) * mm, "end": v(9.17, 54.45) * mm});
            skLineSegment(sketch, "E335", {"start": v(9.17, 54.45) * mm, "end": v(9.13, 54.75) * mm});
            skLineSegment(sketch, "E336", {"start": v(9.13, 54.75) * mm, "end": v(9.09, 55.07) * mm});
            skLineSegment(sketch, "E337", {"start": v(9.09, 55.07) * mm, "end": v(9.03, 55.42) * mm});
            skLineSegment(sketch, "E338", {"start": v(9.03, 55.42) * mm, "end": v(8.96, 55.78) * mm});
            skLineSegment(sketch, "E339", {"start": v(8.96, 55.78) * mm, "end": v(8.89, 56.16) * mm});
            skLineSegment(sketch, "E340", {"start": v(8.89, 56.16) * mm, "end": v(8.8, 56.55) * mm});
            skLineSegment(sketch, "E341", {"start": v(8.8, 56.55) * mm, "end": v(8.7, 56.97) * mm});
            skLineSegment(sketch, "E342", {"start": v(8.7, 56.97) * mm, "end": v(8.58, 57.4) * mm});
            skLineSegment(sketch, "E343", {"start": v(8.58, 57.4) * mm, "end": v(8.45, 57.85) * mm});
            skLineSegment(sketch, "E344", {"start": v(8.45, 57.85) * mm, "end": v(8.3, 58.31) * mm});
            skLineSegment(sketch, "E345", {"start": v(8.3, 58.31) * mm, "end": v(8.15, 58.8) * mm});
            skLineSegment(sketch, "E346", {"start": v(8.15, 58.8) * mm, "end": v(7.97, 59.3) * mm});
            skLineSegment(sketch, "E347", {"start": v(7.97, 59.3) * mm, "end": v(7.78, 59.8) * mm});
            skLineSegment(sketch, "E348", {"start": v(7.78, 59.8) * mm, "end": v(7.58, 60.33) * mm});
            skLineSegment(sketch, "E349", {"start": v(7.58, 60.33) * mm, "end": v(7.35, 60.87) * mm});
            skLineSegment(sketch, "E350", {"start": v(7.35, 60.87) * mm, "end": v(7.1, 61.43) * mm});
            skLineSegment(sketch, "E351", {"start": v(7.1, 61.43) * mm, "end": v(6.84, 62) * mm});
            skLineSegment(sketch, "E352", {"start": v(6.84, 62) * mm, "end": v(6.56, 62.58) * mm});
            skLineSegment(sketch, "E353", {"start": v(6.56, 62.58) * mm, "end": v(6.25, 63.17) * mm});
            skLineSegment(sketch, "E354", {"start": v(6.25, 63.17) * mm, "end": v(5.93, 63.77) * mm});
            skLineSegment(sketch, "E355", {"start": v(5.93, 63.77) * mm, "end": v(5.58, 64.4) * mm});
            skLineSegment(sketch, "E356", {"start": v(5.58, 64.4) * mm, "end": v(5.22, 65.02) * mm});
            skLineSegment(sketch, "E357", {"start": v(5.22, 65.02) * mm, "end": v(4.83, 65.65) * mm});
            skLineSegment(sketch, "E358", {"start": v(4.83, 65.65) * mm, "end": v(4.4, 66) * mm});
            skLineSegment(sketch, "E359", {"start": v(4.4, 66) * mm, "end": v(2.28, 66.1) * mm});
            skLineSegment(sketch, "E360", {"start": v(2.28, 66.1) * mm, "end": v(1.81, 65.8) * mm});
            skLineSegment(sketch, "E361", {"start": v(1.81, 65.8) * mm, "end": v(1.36, 65.21) * mm});
            skLineSegment(sketch, "E362", {"start": v(1.36, 65.21) * mm, "end": v(0.93, 64.62) * mm});
            skLineSegment(sketch, "E363", {"start": v(0.93, 64.62) * mm, "end": v(0.52, 64.05) * mm});
            skLineSegment(sketch, "E364", {"start": v(0.52, 64.05) * mm, "end": v(0.14, 63.48) * mm});
            skLineSegment(sketch, "E365", {"start": v(0.14, 63.48) * mm, "end": v(-0.22, 62.92) * mm});
            skLineSegment(sketch, "E366", {"start": v(-0.22, 62.92) * mm, "end": v(-0.56, 62.37) * mm});
            skLineSegment(sketch, "E367", {"start": v(-0.56, 62.37) * mm, "end": v(-0.88, 61.83) * mm});
            skLineSegment(sketch, "E368", {"start": v(-0.88, 61.83) * mm, "end": v(-1.18, 61.3) * mm});
            skLineSegment(sketch, "E369", {"start": v(-1.18, 61.3) * mm, "end": v(-1.46, 60.79) * mm});
            skLineSegment(sketch, "E370", {"start": v(-1.46, 60.79) * mm, "end": v(-1.72, 60.28) * mm});
            skLineSegment(sketch, "E371", {"start": v(-1.72, 60.28) * mm, "end": v(-1.96, 59.8) * mm});
            skLineSegment(sketch, "E372", {"start": v(-1.96, 59.8) * mm, "end": v(-2.18, 59.32) * mm});
            skLineSegment(sketch, "E373", {"start": v(-2.18, 59.32) * mm, "end": v(-2.4, 58.85) * mm});
            skLineSegment(sketch, "E374", {"start": v(-2.4, 58.85) * mm, "end": v(-2.58, 58.4) * mm});
            skLineSegment(sketch, "E375", {"start": v(-2.58, 58.4) * mm, "end": v(-2.75, 57.97) * mm});
            skLineSegment(sketch, "E376", {"start": v(-2.75, 57.97) * mm, "end": v(-2.91, 57.55) * mm});
            skLineSegment(sketch, "E377", {"start": v(-2.91, 57.55) * mm, "end": v(-3.05, 57.15) * mm});
            skLineSegment(sketch, "E378", {"start": v(-3.05, 57.15) * mm, "end": v(-3.18, 56.77) * mm});
            skLineSegment(sketch, "E379", {"start": v(-3.18, 56.77) * mm, "end": v(-3.3, 56.4) * mm});
            skLineSegment(sketch, "E380", {"start": v(-3.3, 56.4) * mm, "end": v(-3.4, 56.04) * mm});
            skLineSegment(sketch, "E381", {"start": v(-3.4, 56.04) * mm, "end": v(-3.5, 55.7) * mm});
            skLineSegment(sketch, "E382", {"start": v(-3.5, 55.7) * mm, "end": v(-3.57, 55.4) * mm});
            skLineSegment(sketch, "E383", {"start": v(-3.57, 55.4) * mm, "end": v(-3.64, 55.1) * mm});
            skLineSegment(sketch, "E384", {"start": v(-3.64, 55.1) * mm, "end": v(-3.7, 54.81) * mm});
            skLineSegment(sketch, "E385", {"start": v(-3.7, 54.81) * mm, "end": v(-3.75, 54.55) * mm});
            skLineSegment(sketch, "E386", {"start": v(-3.75, 54.55) * mm, "end": v(-3.79, 54.3) * mm});
            skLineSegment(sketch, "E387", {"start": v(-3.79, 54.3) * mm, "end": v(-3.82, 54.08) * mm});
            skLineSegment(sketch, "E388", {"start": v(-3.82, 54.08) * mm, "end": v(-3.85, 53.87) * mm});
            skLineSegment(sketch, "E389", {"start": v(-3.85, 53.87) * mm, "end": v(-3.87, 53.69) * mm});
            skLineSegment(sketch, "E390", {"start": v(-3.87, 53.69) * mm, "end": v(-3.88, 53.52) * mm});
            skLineSegment(sketch, "E391", {"start": v(-3.88, 53.52) * mm, "end": v(-3.9, 53.37) * mm});
            skLineSegment(sketch, "E392", {"start": v(-3.9, 53.37) * mm, "end": v(-3.9, 53.25) * mm});
            skLineSegment(sketch, "E393", {"start": v(-3.9, 53.25) * mm, "end": v(-3.9, 53.14) * mm});
            skLineSegment(sketch, "E394", {"start": v(-3.9, 53.14) * mm, "end": v(-3.9, 53.05) * mm});
            skLineSegment(sketch, "E395", {"start": v(-3.9, 53.05) * mm, "end": v(-3.9, 52.98) * mm});
            skLineSegment(sketch, "E396", {"start": v(-3.9, 52.98) * mm, "end": v(-3.9, 52.93) * mm});
            skLineSegment(sketch, "E397", {"start": v(-3.9, 52.93) * mm, "end": v(-3.9, 52.9) * mm});
            skLineSegment(sketch, "E398", {"start": v(-3.9, 52.9) * mm, "end": v(-3.82, 51.78) * mm});
            skLineSegment(sketch, "E399", {"start": v(-3.82, 51.78) * mm, "end": v(-9.02, 51.14) * mm});
            skLineSegment(sketch, "E400", {"start": v(-9.02, 51.14) * mm, "end": v(-9.21, 52.24) * mm});
            skLineSegment(sketch, "E401", {"start": v(-9.21, 52.24) * mm, "end": v(-9.22, 52.27) * mm});
            skLineSegment(sketch, "E402", {"start": v(-9.22, 52.27) * mm, "end": v(-9.23, 52.32) * mm});
            skLineSegment(sketch, "E403", {"start": v(-9.23, 52.32) * mm, "end": v(-9.25, 52.38) * mm});
            skLineSegment(sketch, "E404", {"start": v(-9.25, 52.38) * mm, "end": v(-9.27, 52.47) * mm});
            skLineSegment(sketch, "E405", {"start": v(-9.27, 52.47) * mm, "end": v(-9.3, 52.57) * mm});
            skLineSegment(sketch, "E406", {"start": v(-9.3, 52.57) * mm, "end": v(-9.33, 52.7) * mm});
            skLineSegment(sketch, "E407", {"start": v(-9.33, 52.7) * mm, "end": v(-9.38, 52.84) * mm});
            skLineSegment(sketch, "E408", {"start": v(-9.38, 52.84) * mm, "end": v(-9.44, 53) * mm});
            skLineSegment(sketch, "E409", {"start": v(-9.44, 53) * mm, "end": v(-9.5, 53.17) * mm});
            skLineSegment(sketch, "E410", {"start": v(-9.5, 53.17) * mm, "end": v(-9.58, 53.36) * mm});
            skLineSegment(sketch, "E411", {"start": v(-9.58, 53.36) * mm, "end": v(-9.67, 53.57) * mm});
            skLineSegment(sketch, "E412", {"start": v(-9.67, 53.57) * mm, "end": v(-9.76, 53.8) * mm});
            skLineSegment(sketch, "E413", {"start": v(-9.76, 53.8) * mm, "end": v(-9.88, 54.04) * mm});
            skLineSegment(sketch, "E414", {"start": v(-9.88, 54.04) * mm, "end": v(-10, 54.3) * mm});
            skLineSegment(sketch, "E415", {"start": v(-10, 54.3) * mm, "end": v(-10.14, 54.57) * mm});
            skLineSegment(sketch, "E416", {"start": v(-10.14, 54.57) * mm, "end": v(-10.3, 54.86) * mm});
            skLineSegment(sketch, "E417", {"start": v(-10.3, 54.86) * mm, "end": v(-10.47, 55.16) * mm});
            skLineSegment(sketch, "E418", {"start": v(-10.47, 55.16) * mm, "end": v(-10.65, 55.48) * mm});
            skLineSegment(sketch, "E419", {"start": v(-10.65, 55.48) * mm, "end": v(-10.86, 55.8) * mm});
            skLineSegment(sketch, "E420", {"start": v(-10.86, 55.8) * mm, "end": v(-11.08, 56.15) * mm});
            skLineSegment(sketch, "E421", {"start": v(-11.08, 56.15) * mm, "end": v(-11.31, 56.5) * mm});
            skLineSegment(sketch, "E422", {"start": v(-11.31, 56.5) * mm, "end": v(-11.57, 56.87) * mm});
            skLineSegment(sketch, "E423", {"start": v(-11.57, 56.87) * mm, "end": v(-11.84, 57.25) * mm});
            skLineSegment(sketch, "E424", {"start": v(-11.84, 57.25) * mm, "end": v(-12.14, 57.64) * mm});
            skLineSegment(sketch, "E425", {"start": v(-12.14, 57.64) * mm, "end": v(-12.45, 58.04) * mm});
            skLineSegment(sketch, "E426", {"start": v(-12.45, 58.04) * mm, "end": v(-12.79, 58.44) * mm});
            skLineSegment(sketch, "E427", {"start": v(-12.79, 58.44) * mm, "end": v(-13.14, 58.86) * mm});
            skLineSegment(sketch, "E428", {"start": v(-13.14, 58.86) * mm, "end": v(-13.52, 59.28) * mm});
            skLineSegment(sketch, "E429", {"start": v(-13.52, 59.28) * mm, "end": v(-13.91, 59.71) * mm});
            skLineSegment(sketch, "E430", {"start": v(-13.91, 59.71) * mm, "end": v(-14.33, 60.15) * mm});
            skLineSegment(sketch, "E431", {"start": v(-14.33, 60.15) * mm, "end": v(-14.78, 60.6) * mm});
            skLineSegment(sketch, "E432", {"start": v(-14.78, 60.6) * mm, "end": v(-15.24, 61.05) * mm});
            skLineSegment(sketch, "E433", {"start": v(-15.24, 61.05) * mm, "end": v(-15.73, 61.5) * mm});
            skLineSegment(sketch, "E434", {"start": v(-15.73, 61.5) * mm, "end": v(-16.24, 61.96) * mm});
            skLineSegment(sketch, "E435", {"start": v(-16.24, 61.96) * mm, "end": v(-16.77, 62.42) * mm});
            skLineSegment(sketch, "E436", {"start": v(-16.77, 62.42) * mm, "end": v(-17.34, 62.88) * mm});
            skLineSegment(sketch, "E437", {"start": v(-17.34, 62.88) * mm, "end": v(-17.92, 63.34) * mm});
            skLineSegment(sketch, "E438", {"start": v(-17.92, 63.34) * mm, "end": v(-18.44, 63.52) * mm});
            skLineSegment(sketch, "E439", {"start": v(-18.44, 63.52) * mm, "end": v(-20.47, 62.9) * mm});
            skLineSegment(sketch, "E440", {"start": v(-20.47, 62.9) * mm, "end": v(-20.8, 62.46) * mm});
            skLineSegment(sketch, "E441", {"start": v(-20.8, 62.46) * mm, "end": v(-21.02, 61.74) * mm});
            skLineSegment(sketch, "E442", {"start": v(-21.02, 61.74) * mm, "end": v(-21.23, 61.05) * mm});
            skLineSegment(sketch, "E443", {"start": v(-21.23, 61.05) * mm, "end": v(-21.41, 60.36) * mm});
            skLineSegment(sketch, "E444", {"start": v(-21.41, 60.36) * mm, "end": v(-21.58, 59.7) * mm});
            skLineSegment(sketch, "E445", {"start": v(-21.58, 59.7) * mm, "end": v(-21.73, 59.05) * mm});
            skLineSegment(sketch, "E446", {"start": v(-21.73, 59.05) * mm, "end": v(-21.86, 58.42) * mm});
            skLineSegment(sketch, "E447", {"start": v(-21.86, 58.42) * mm, "end": v(-21.97, 57.8) * mm});
            skLineSegment(sketch, "E448", {"start": v(-21.97, 57.8) * mm, "end": v(-22.07, 57.2) * mm});
            skLineSegment(sketch, "E449", {"start": v(-22.07, 57.2) * mm, "end": v(-22.16, 56.62) * mm});
            skLineSegment(sketch, "E450", {"start": v(-22.16, 56.62) * mm, "end": v(-22.23, 56.06) * mm});
            skLineSegment(sketch, "E451", {"start": v(-22.23, 56.06) * mm, "end": v(-22.3, 55.52) * mm});
            skLineSegment(sketch, "E452", {"start": v(-22.3, 55.52) * mm, "end": v(-22.34, 55) * mm});
            skLineSegment(sketch, "E453", {"start": v(-22.34, 55) * mm, "end": v(-22.38, 54.49) * mm});
            skLineSegment(sketch, "E454", {"start": v(-22.38, 54.49) * mm, "end": v(-22.4, 54) * mm});
            skLineSegment(sketch, "E455", {"start": v(-22.4, 54) * mm, "end": v(-22.42, 53.54) * mm});
            skLineSegment(sketch, "E456", {"start": v(-22.42, 53.54) * mm, "end": v(-22.42, 53.09) * mm});
            skLineSegment(sketch, "E457", {"start": v(-22.42, 53.09) * mm, "end": v(-22.42, 52.66) * mm});
            skLineSegment(sketch, "E458", {"start": v(-22.42, 52.66) * mm, "end": v(-22.4, 52.25) * mm});
            skLineSegment(sketch, "E459", {"start": v(-22.4, 52.25) * mm, "end": v(-22.39, 51.87) * mm});
            skLineSegment(sketch, "E460", {"start": v(-22.39, 51.87) * mm, "end": v(-22.36, 51.5) * mm});
            skLineSegment(sketch, "E461", {"start": v(-22.36, 51.5) * mm, "end": v(-22.33, 51.16) * mm});
            skLineSegment(sketch, "E462", {"start": v(-22.33, 51.16) * mm, "end": v(-22.3, 50.83) * mm});
            skLineSegment(sketch, "E463", {"start": v(-22.3, 50.83) * mm, "end": v(-22.26, 50.53) * mm});
            skLineSegment(sketch, "E464", {"start": v(-22.26, 50.53) * mm, "end": v(-22.22, 50.24) * mm});
            skLineSegment(sketch, "E465", {"start": v(-22.22, 50.24) * mm, "end": v(-22.18, 49.98) * mm});
            skLineSegment(sketch, "E466", {"start": v(-22.18, 49.98) * mm, "end": v(-22.13, 49.73) * mm});
            skLineSegment(sketch, "E467", {"start": v(-22.13, 49.73) * mm, "end": v(-22.09, 49.51) * mm});
            skLineSegment(sketch, "E468", {"start": v(-22.09, 49.51) * mm, "end": v(-22.04, 49.3) * mm});
            skLineSegment(sketch, "E469", {"start": v(-22.04, 49.3) * mm, "end": v(-22, 49.13) * mm});
            skLineSegment(sketch, "E470", {"start": v(-22, 49.13) * mm, "end": v(-21.95, 48.96) * mm});
            skLineSegment(sketch, "E471", {"start": v(-21.95, 48.96) * mm, "end": v(-21.91, 48.82) * mm});
            skLineSegment(sketch, "E472", {"start": v(-21.91, 48.82) * mm, "end": v(-21.88, 48.7) * mm});
            skLineSegment(sketch, "E473", {"start": v(-21.88, 48.7) * mm, "end": v(-21.84, 48.6) * mm});
            skLineSegment(sketch, "E474", {"start": v(-21.84, 48.6) * mm, "end": v(-21.81, 48.52) * mm});
            skLineSegment(sketch, "E475", {"start": v(-21.81, 48.52) * mm, "end": v(-21.79, 48.45) * mm});
            skLineSegment(sketch, "E476", {"start": v(-21.79, 48.45) * mm, "end": v(-21.77, 48.4) * mm});
            skLineSegment(sketch, "E477", {"start": v(-21.77, 48.4) * mm, "end": v(-21.76, 48.38) * mm});
            skLineSegment(sketch, "E478", {"start": v(-21.76, 48.38) * mm, "end": v(-21.3, 47.35) * mm});
            skLineSegment(sketch, "E479", {"start": v(-21.3, 47.35) * mm, "end": v(-25.96, 44.97) * mm});
            skLineSegment(sketch, "E480", {"start": v(-25.96, 44.97) * mm, "end": v(-26.53, 45.94) * mm});
            skLineSegment(sketch, "E481", {"start": v(-26.53, 45.94) * mm, "end": v(-26.54, 45.97) * mm});
            skLineSegment(sketch, "E482", {"start": v(-26.54, 45.97) * mm, "end": v(-26.57, 46) * mm});
            skLineSegment(sketch, "E483", {"start": v(-26.57, 46) * mm, "end": v(-26.6, 46.06) * mm});
            skLineSegment(sketch, "E484", {"start": v(-26.6, 46.06) * mm, "end": v(-26.65, 46.14) * mm});
            skLineSegment(sketch, "E485", {"start": v(-26.65, 46.14) * mm, "end": v(-26.72, 46.22) * mm});
            skLineSegment(sketch, "E486", {"start": v(-26.72, 46.22) * mm, "end": v(-26.8, 46.32) * mm});
            skLineSegment(sketch, "E487", {"start": v(-26.8, 46.32) * mm, "end": v(-26.89, 46.44) * mm});
            skLineSegment(sketch, "E488", {"start": v(-26.89, 46.44) * mm, "end": v(-27, 46.57) * mm});
            skLineSegment(sketch, "E489", {"start": v(-27, 46.57) * mm, "end": v(-27.11, 46.71) * mm});
            skLineSegment(sketch, "E490", {"start": v(-27.11, 46.71) * mm, "end": v(-27.25, 46.87) * mm});
            skLineSegment(sketch, "E491", {"start": v(-27.25, 46.87) * mm, "end": v(-27.4, 47.03) * mm});
            skLineSegment(sketch, "E492", {"start": v(-27.4, 47.03) * mm, "end": v(-27.58, 47.21) * mm});
            skLineSegment(sketch, "E493", {"start": v(-27.58, 47.21) * mm, "end": v(-27.76, 47.4) * mm});
            skLineSegment(sketch, "E494", {"start": v(-27.76, 47.4) * mm, "end": v(-27.97, 47.6) * mm});
            skLineSegment(sketch, "E495", {"start": v(-27.97, 47.6) * mm, "end": v(-28.2, 47.81) * mm});
            skLineSegment(sketch, "E496", {"start": v(-28.2, 47.81) * mm, "end": v(-28.44, 48.03) * mm});
            skLineSegment(sketch, "E497", {"start": v(-28.44, 48.03) * mm, "end": v(-28.7, 48.26) * mm});
            skLineSegment(sketch, "E498", {"start": v(-28.7, 48.26) * mm, "end": v(-28.99, 48.49) * mm});
            skLineSegment(sketch, "E499", {"start": v(-28.99, 48.49) * mm, "end": v(-29.3, 48.73) * mm});
            skLineSegment(sketch, "E500", {"start": v(-29.3, 48.73) * mm, "end": v(-29.61, 48.98) * mm});
            skLineSegment(sketch, "E501", {"start": v(-29.61, 48.98) * mm, "end": v(-29.96, 49.23) * mm});
            skLineSegment(sketch, "E502", {"start": v(-29.96, 49.23) * mm, "end": v(-30.32, 49.49) * mm});
            skLineSegment(sketch, "E503", {"start": v(-30.32, 49.49) * mm, "end": v(-30.71, 49.75) * mm});
            skLineSegment(sketch, "E504", {"start": v(-30.71, 49.75) * mm, "end": v(-31.12, 50.01) * mm});
            skLineSegment(sketch, "E505", {"start": v(-31.12, 50.01) * mm, "end": v(-31.55, 50.28) * mm});
            skLineSegment(sketch, "E506", {"start": v(-31.55, 50.28) * mm, "end": v(-32, 50.55) * mm});
            skLineSegment(sketch, "E507", {"start": v(-32, 50.55) * mm, "end": v(-32.48, 50.82) * mm});
            skLineSegment(sketch, "E508", {"start": v(-32.48, 50.82) * mm, "end": v(-32.98, 51.09) * mm});
            skLineSegment(sketch, "E509", {"start": v(-32.98, 51.09) * mm, "end": v(-33.5, 51.36) * mm});
            skLineSegment(sketch, "E510", {"start": v(-33.5, 51.36) * mm, "end": v(-34.04, 51.62) * mm});
            skLineSegment(sketch, "E511", {"start": v(-34.04, 51.62) * mm, "end": v(-34.6, 51.89) * mm});
            skLineSegment(sketch, "E512", {"start": v(-34.6, 51.89) * mm, "end": v(-35.2, 52.15) * mm});
            skLineSegment(sketch, "E513", {"start": v(-35.2, 52.15) * mm, "end": v(-35.81, 52.41) * mm});
            skLineSegment(sketch, "E514", {"start": v(-35.81, 52.41) * mm, "end": v(-36.45, 52.67) * mm});
            skLineSegment(sketch, "E515", {"start": v(-36.45, 52.67) * mm, "end": v(-37.11, 52.92) * mm});
            skLineSegment(sketch, "E516", {"start": v(-37.11, 52.92) * mm, "end": v(-37.8, 53.16) * mm});
            skLineSegment(sketch, "E517", {"start": v(-37.8, 53.16) * mm, "end": v(-38.5, 53.4) * mm});
            skLineSegment(sketch, "E518", {"start": v(-38.5, 53.4) * mm, "end": v(-39.06, 53.38) * mm});
            skLineSegment(sketch, "E519", {"start": v(-39.06, 53.38) * mm, "end": v(-40.75, 52.1) * mm});
            skLineSegment(sketch, "E520", {"start": v(-40.75, 52.1) * mm, "end": v(-40.9, 51.57) * mm});
            skLineSegment(sketch, "E521", {"start": v(-40.9, 51.57) * mm, "end": v(-40.87, 50.83) * mm});
            skLineSegment(sketch, "E522", {"start": v(-40.87, 50.83) * mm, "end": v(-40.83, 50.1) * mm});
            skLineSegment(sketch, "E523", {"start": v(-40.83, 50.1) * mm, "end": v(-40.77, 49.4) * mm});
            skLineSegment(sketch, "E524", {"start": v(-40.77, 49.4) * mm, "end": v(-40.7, 48.72) * mm});
            skLineSegment(sketch, "E525", {"start": v(-40.7, 48.72) * mm, "end": v(-40.61, 48.06) * mm});
            skLineSegment(sketch, "E526", {"start": v(-40.61, 48.06) * mm, "end": v(-40.52, 47.42) * mm});
            skLineSegment(sketch, "E527", {"start": v(-40.52, 47.42) * mm, "end": v(-40.42, 46.8) * mm});
            skLineSegment(sketch, "E528", {"start": v(-40.42, 46.8) * mm, "end": v(-40.3, 46.2) * mm});
            skLineSegment(sketch, "E529", {"start": v(-40.3, 46.2) * mm, "end": v(-40.2, 45.63) * mm});
            skLineSegment(sketch, "E530", {"start": v(-40.2, 45.63) * mm, "end": v(-40.07, 45.08) * mm});
            skLineSegment(sketch, "E531", {"start": v(-40.07, 45.08) * mm, "end": v(-39.94, 44.55) * mm});
            skLineSegment(sketch, "E532", {"start": v(-39.94, 44.55) * mm, "end": v(-39.8, 44.03) * mm});
            skLineSegment(sketch, "E533", {"start": v(-39.8, 44.03) * mm, "end": v(-39.66, 43.55) * mm});
            skLineSegment(sketch, "E534", {"start": v(-39.66, 43.55) * mm, "end": v(-39.52, 43.08) * mm});
            skLineSegment(sketch, "E535", {"start": v(-39.52, 43.08) * mm, "end": v(-39.37, 42.64) * mm});
            skLineSegment(sketch, "E536", {"start": v(-39.37, 42.64) * mm, "end": v(-39.22, 42.22) * mm});
            skLineSegment(sketch, "E537", {"start": v(-39.22, 42.22) * mm, "end": v(-39.08, 41.82) * mm});
            skLineSegment(sketch, "E538", {"start": v(-39.08, 41.82) * mm, "end": v(-38.93, 41.44) * mm});
            skLineSegment(sketch, "E539", {"start": v(-38.93, 41.44) * mm, "end": v(-38.78, 41.08) * mm});
            skLineSegment(sketch, "E540", {"start": v(-38.78, 41.08) * mm, "end": v(-38.63, 40.75) * mm});
            skLineSegment(sketch, "E541", {"start": v(-38.63, 40.75) * mm, "end": v(-38.48, 40.43) * mm});
            skLineSegment(sketch, "E542", {"start": v(-38.48, 40.43) * mm, "end": v(-38.34, 40.14) * mm});
            skLineSegment(sketch, "E543", {"start": v(-38.34, 40.14) * mm, "end": v(-38.2, 39.86) * mm});
            skLineSegment(sketch, "E544", {"start": v(-38.2, 39.86) * mm, "end": v(-38.06, 39.61) * mm});
            skLineSegment(sketch, "E545", {"start": v(-38.06, 39.61) * mm, "end": v(-37.93, 39.38) * mm});
            skLineSegment(sketch, "E546", {"start": v(-37.93, 39.38) * mm, "end": v(-37.8, 39.17) * mm});
            skLineSegment(sketch, "E547", {"start": v(-37.8, 39.17) * mm, "end": v(-37.69, 38.97) * mm});
            skLineSegment(sketch, "E548", {"start": v(-37.69, 38.97) * mm, "end": v(-37.58, 38.8) * mm});
            skLineSegment(sketch, "E549", {"start": v(-37.58, 38.8) * mm, "end": v(-37.47, 38.64) * mm});
            skLineSegment(sketch, "E550", {"start": v(-37.47, 38.64) * mm, "end": v(-37.38, 38.5) * mm});
            skLineSegment(sketch, "E551", {"start": v(-37.38, 38.5) * mm, "end": v(-37.3, 38.38) * mm});
            skLineSegment(sketch, "E552", {"start": v(-37.3, 38.38) * mm, "end": v(-37.21, 38.28) * mm});
            skLineSegment(sketch, "E553", {"start": v(-37.21, 38.28) * mm, "end": v(-37.15, 38.2) * mm});
            skLineSegment(sketch, "E554", {"start": v(-37.15, 38.2) * mm, "end": v(-37.1, 38.13) * mm});
            skLineSegment(sketch, "E555", {"start": v(-37.1, 38.13) * mm, "end": v(-37.05, 38.08) * mm});
            skLineSegment(sketch, "E556", {"start": v(-37.05, 38.08) * mm, "end": v(-37.02, 38.04) * mm});
            skLineSegment(sketch, "E557", {"start": v(-37.02, 38.04) * mm, "end": v(-37, 38.02) * mm});
            skLineSegment(sketch, "E558", {"start": v(-37, 38.02) * mm, "end": v(-36.21, 37.21) * mm});
            skLineSegment(sketch, "E559", {"start": v(-36.21, 37.21) * mm, "end": v(-39.78, 33.38) * mm});
            skLineSegment(sketch, "E560", {"start": v(-39.78, 33.38) * mm, "end": v(-40.64, 34.1) * mm});
            skLineSegment(sketch, "E561", {"start": v(-40.64, 34.1) * mm, "end": v(-40.66, 34.12) * mm});
            skLineSegment(sketch, "E562", {"start": v(-40.66, 34.12) * mm, "end": v(-40.7, 34.15) * mm});
            skLineSegment(sketch, "E563", {"start": v(-40.7, 34.15) * mm, "end": v(-40.75, 34.19) * mm});
            skLineSegment(sketch, "E564", {"start": v(-40.75, 34.19) * mm, "end": v(-40.83, 34.24) * mm});
            skLineSegment(sketch, "E565", {"start": v(-40.83, 34.24) * mm, "end": v(-40.92, 34.3) * mm});
            skLineSegment(sketch, "E566", {"start": v(-40.92, 34.3) * mm, "end": v(-41.02, 34.37) * mm});
            skLineSegment(sketch, "E567", {"start": v(-41.02, 34.37) * mm, "end": v(-41.15, 34.44) * mm});
            skLineSegment(sketch, "E568", {"start": v(-41.15, 34.44) * mm, "end": v(-41.3, 34.53) * mm});
            skLineSegment(sketch, "E569", {"start": v(-41.3, 34.53) * mm, "end": v(-41.46, 34.62) * mm});
            skLineSegment(sketch, "E570", {"start": v(-41.46, 34.62) * mm, "end": v(-41.64, 34.72) * mm});
            skLineSegment(sketch, "E571", {"start": v(-41.64, 34.72) * mm, "end": v(-41.84, 34.83) * mm});
            skLineSegment(sketch, "E572", {"start": v(-41.84, 34.83) * mm, "end": v(-42.06, 34.93) * mm});
            skLineSegment(sketch, "E573", {"start": v(-42.06, 34.93) * mm, "end": v(-42.3, 35.05) * mm});
            skLineSegment(sketch, "E574", {"start": v(-42.3, 35.05) * mm, "end": v(-42.57, 35.16) * mm});
            skLineSegment(sketch, "E575", {"start": v(-42.57, 35.16) * mm, "end": v(-42.85, 35.28) * mm});
            skLineSegment(sketch, "E576", {"start": v(-42.85, 35.28) * mm, "end": v(-43.15, 35.4) * mm});
            skLineSegment(sketch, "E577", {"start": v(-43.15, 35.4) * mm, "end": v(-43.48, 35.53) * mm});
            skLineSegment(sketch, "E578", {"start": v(-43.48, 35.53) * mm, "end": v(-43.82, 35.65) * mm});
            skLineSegment(sketch, "E579", {"start": v(-43.82, 35.65) * mm, "end": v(-44.2, 35.77) * mm});
            skLineSegment(sketch, "E580", {"start": v(-44.2, 35.77) * mm, "end": v(-44.58, 35.9) * mm});
            skLineSegment(sketch, "E581", {"start": v(-44.58, 35.9) * mm, "end": v(-44.99, 36.01) * mm});
            skLineSegment(sketch, "E582", {"start": v(-44.99, 36.01) * mm, "end": v(-45.42, 36.13) * mm});
            skLineSegment(sketch, "E583", {"start": v(-45.42, 36.13) * mm, "end": v(-45.87, 36.24) * mm});
            skLineSegment(sketch, "E584", {"start": v(-45.87, 36.24) * mm, "end": v(-46.35, 36.35) * mm});
            skLineSegment(sketch, "E585", {"start": v(-46.35, 36.35) * mm, "end": v(-46.84, 36.45) * mm});
            skLineSegment(sketch, "E586", {"start": v(-46.84, 36.45) * mm, "end": v(-47.36, 36.55) * mm});
            skLineSegment(sketch, "E587", {"start": v(-47.36, 36.55) * mm, "end": v(-47.9, 36.64) * mm});
            skLineSegment(sketch, "E588", {"start": v(-47.9, 36.64) * mm, "end": v(-48.46, 36.73) * mm});
            skLineSegment(sketch, "E589", {"start": v(-48.46, 36.73) * mm, "end": v(-49.04, 36.8) * mm});
            skLineSegment(sketch, "E590", {"start": v(-49.04, 36.8) * mm, "end": v(-49.65, 36.87) * mm});
            skLineSegment(sketch, "E591", {"start": v(-49.65, 36.87) * mm, "end": v(-50.27, 36.92) * mm});
            skLineSegment(sketch, "E592", {"start": v(-50.27, 36.92) * mm, "end": v(-50.91, 36.97) * mm});
            skLineSegment(sketch, "E593", {"start": v(-50.91, 36.97) * mm, "end": v(-51.58, 37) * mm});
            skLineSegment(sketch, "E594", {"start": v(-51.58, 37) * mm, "end": v(-52.26, 37.02) * mm});
            skLineSegment(sketch, "E595", {"start": v(-52.26, 37.02) * mm, "end": v(-52.97, 37.03) * mm});
            skLineSegment(sketch, "E596", {"start": v(-52.97, 37.03) * mm, "end": v(-53.7, 37.03) * mm});
            skLineSegment(sketch, "E597", {"start": v(-53.7, 37.03) * mm, "end": v(-54.44, 37) * mm});
            skLineSegment(sketch, "E598", {"start": v(-54.44, 37) * mm, "end": v(-54.96, 36.8) * mm});
            skLineSegment(sketch, "E599", {"start": v(-54.96, 36.8) * mm, "end": v(-56.11, 35.03) * mm});
            skLineSegment(sketch, "E600", {"start": v(-56.11, 35.03) * mm, "end": v(-56.08, 34.47) * mm});
            skLineSegment(sketch, "E601", {"start": v(-56.08, 34.47) * mm, "end": v(-55.8, 33.78) * mm});
            skLineSegment(sketch, "E602", {"start": v(-55.8, 33.78) * mm, "end": v(-55.5, 33.12) * mm});
            skLineSegment(sketch, "E603", {"start": v(-55.5, 33.12) * mm, "end": v(-55.2, 32.48) * mm});
            skLineSegment(sketch, "E604", {"start": v(-55.2, 32.48) * mm, "end": v(-54.9, 31.86) * mm});
            skLineSegment(sketch, "E605", {"start": v(-54.9, 31.86) * mm, "end": v(-54.6, 31.27) * mm});
            skLineSegment(sketch, "E606", {"start": v(-54.6, 31.27) * mm, "end": v(-54.3, 30.7) * mm});
            skLineSegment(sketch, "E607", {"start": v(-54.3, 30.7) * mm, "end": v(-53.99, 30.15) * mm});
            skLineSegment(sketch, "E608", {"start": v(-53.99, 30.15) * mm, "end": v(-53.68, 29.63) * mm});
            skLineSegment(sketch, "E609", {"start": v(-53.68, 29.63) * mm, "end": v(-53.37, 29.13) * mm});
            skLineSegment(sketch, "E610", {"start": v(-53.37, 29.13) * mm, "end": v(-53.07, 28.65) * mm});
            skLineSegment(sketch, "E611", {"start": v(-53.07, 28.65) * mm, "end": v(-52.76, 28.2) * mm});
            skLineSegment(sketch, "E612", {"start": v(-52.76, 28.2) * mm, "end": v(-52.46, 27.77) * mm});
            skLineSegment(sketch, "E613", {"start": v(-52.46, 27.77) * mm, "end": v(-52.16, 27.36) * mm});
            skLineSegment(sketch, "E614", {"start": v(-52.16, 27.36) * mm, "end": v(-51.87, 26.97) * mm});
            skLineSegment(sketch, "E615", {"start": v(-51.87, 26.97) * mm, "end": v(-51.58, 26.6) * mm});
            skLineSegment(sketch, "E616", {"start": v(-51.58, 26.6) * mm, "end": v(-51.3, 26.26) * mm});
            skLineSegment(sketch, "E617", {"start": v(-51.3, 26.26) * mm, "end": v(-51.02, 25.93) * mm});
            skLineSegment(sketch, "E618", {"start": v(-51.02, 25.93) * mm, "end": v(-50.75, 25.63) * mm});
            skLineSegment(sketch, "E619", {"start": v(-50.75, 25.63) * mm, "end": v(-50.49, 25.34) * mm});
            skLineSegment(sketch, "E620", {"start": v(-50.49, 25.34) * mm, "end": v(-50.24, 25.08) * mm});
            skLineSegment(sketch, "E621", {"start": v(-50.24, 25.08) * mm, "end": v(-50, 24.83) * mm});
            skLineSegment(sketch, "E622", {"start": v(-50, 24.83) * mm, "end": v(-49.76, 24.6) * mm});
            skLineSegment(sketch, "E623", {"start": v(-49.76, 24.6) * mm, "end": v(-49.53, 24.4) * mm});
            skLineSegment(sketch, "E624", {"start": v(-49.53, 24.4) * mm, "end": v(-49.32, 24.2) * mm});
            skLineSegment(sketch, "E625", {"start": v(-49.32, 24.2) * mm, "end": v(-49.11, 24.03) * mm});
            skLineSegment(sketch, "E626", {"start": v(-49.11, 24.03) * mm, "end": v(-48.92, 23.87) * mm});
            skLineSegment(sketch, "E627", {"start": v(-48.92, 23.87) * mm, "end": v(-48.75, 23.73) * mm});
            skLineSegment(sketch, "E628", {"start": v(-48.75, 23.73) * mm, "end": v(-48.58, 23.6) * mm});
            skLineSegment(sketch, "E629", {"start": v(-48.58, 23.6) * mm, "end": v(-48.43, 23.5) * mm});
            skLineSegment(sketch, "E630", {"start": v(-48.43, 23.5) * mm, "end": v(-48.3, 23.4) * mm});
            skLineSegment(sketch, "E631", {"start": v(-48.3, 23.4) * mm, "end": v(-48.17, 23.31) * mm});
            skLineSegment(sketch, "E632", {"start": v(-48.17, 23.31) * mm, "end": v(-48.06, 23.24) * mm});
            skLineSegment(sketch, "E633", {"start": v(-48.06, 23.24) * mm, "end": v(-47.97, 23.19) * mm});
            skLineSegment(sketch, "E634", {"start": v(-47.97, 23.19) * mm, "end": v(-47.9, 23.14) * mm});
            skLineSegment(sketch, "E635", {"start": v(-47.9, 23.14) * mm, "end": v(-47.84, 23.1) * mm});
            skLineSegment(sketch, "E636", {"start": v(-47.84, 23.1) * mm, "end": v(-47.8, 23.09) * mm});
            skLineSegment(sketch, "E637", {"start": v(-47.8, 23.09) * mm, "end": v(-47.77, 23.08) * mm});
            skLineSegment(sketch, "E638", {"start": v(-47.77, 23.08) * mm, "end": v(-46.76, 22.58) * mm});
            skLineSegment(sketch, "E639", {"start": v(-46.76, 22.58) * mm, "end": v(-48.8, 17.76) * mm});
            skLineSegment(sketch, "E640", {"start": v(-48.8, 17.76) * mm, "end": v(-49.85, 18.14) * mm});
            skLineSegment(sketch, "E641", {"start": v(-49.85, 18.14) * mm, "end": v(-49.88, 18.15) * mm});
            skLineSegment(sketch, "E642", {"start": v(-49.88, 18.15) * mm, "end": v(-49.92, 18.17) * mm});
            skLineSegment(sketch, "E643", {"start": v(-49.92, 18.17) * mm, "end": v(-49.99, 18.19) * mm});
            skLineSegment(sketch, "E644", {"start": v(-49.99, 18.19) * mm, "end": v(-50.07, 18.2) * mm});
            skLineSegment(sketch, "E645", {"start": v(-50.07, 18.2) * mm, "end": v(-50.18, 18.24) * mm});
            skLineSegment(sketch, "E646", {"start": v(-50.18, 18.24) * mm, "end": v(-50.3, 18.26) * mm});
            skLineSegment(sketch, "E647", {"start": v(-50.3, 18.26) * mm, "end": v(-50.45, 18.3) * mm});
            skLineSegment(sketch, "E648", {"start": v(-50.45, 18.3) * mm, "end": v(-50.61, 18.33) * mm});
            skLineSegment(sketch, "E649", {"start": v(-50.61, 18.33) * mm, "end": v(-50.8, 18.36) * mm});
            skLineSegment(sketch, "E650", {"start": v(-50.8, 18.36) * mm, "end": v(-51, 18.39) * mm});
            skLineSegment(sketch, "E651", {"start": v(-51, 18.39) * mm, "end": v(-51.23, 18.41) * mm});
            skLineSegment(sketch, "E652", {"start": v(-51.23, 18.41) * mm, "end": v(-51.47, 18.44) * mm});
            skLineSegment(sketch, "E653", {"start": v(-51.47, 18.44) * mm, "end": v(-51.74, 18.47) * mm});
            skLineSegment(sketch, "E654", {"start": v(-51.74, 18.47) * mm, "end": v(-52.03, 18.49) * mm});
            skLineSegment(sketch, "E655", {"start": v(-52.03, 18.49) * mm, "end": v(-52.33, 18.5) * mm});
            skLineSegment(sketch, "E656", {"start": v(-52.33, 18.5) * mm, "end": v(-52.66, 18.51) * mm});
            skLineSegment(sketch, "E657", {"start": v(-52.66, 18.51) * mm, "end": v(-53, 18.52) * mm});
            skLineSegment(sketch, "E658", {"start": v(-53, 18.52) * mm, "end": v(-53.37, 18.51) * mm});
            skLineSegment(sketch, "E659", {"start": v(-53.37, 18.51) * mm, "end": v(-53.76, 18.5) * mm});
            skLineSegment(sketch, "E660", {"start": v(-53.76, 18.5) * mm, "end": v(-54.17, 18.48) * mm});
            skLineSegment(sketch, "E661", {"start": v(-54.17, 18.48) * mm, "end": v(-54.6, 18.45) * mm});
            skLineSegment(sketch, "E662", {"start": v(-54.6, 18.45) * mm, "end": v(-55.04, 18.42) * mm});
            skLineSegment(sketch, "E663", {"start": v(-55.04, 18.42) * mm, "end": v(-55.5, 18.37) * mm});
            skLineSegment(sketch, "E664", {"start": v(-55.5, 18.37) * mm, "end": v(-55.99, 18.3) * mm});
            skLineSegment(sketch, "E665", {"start": v(-55.99, 18.3) * mm, "end": v(-56.49, 18.24) * mm});
            skLineSegment(sketch, "E666", {"start": v(-56.49, 18.24) * mm, "end": v(-57, 18.15) * mm});
            skLineSegment(sketch, "E667", {"start": v(-57, 18.15) * mm, "end": v(-57.54, 18.05) * mm});
            skLineSegment(sketch, "E668", {"start": v(-57.54, 18.05) * mm, "end": v(-58.1, 17.94) * mm});
            skLineSegment(sketch, "E669", {"start": v(-58.1, 17.94) * mm, "end": v(-58.67, 17.8) * mm});
            skLineSegment(sketch, "E670", {"start": v(-58.67, 17.8) * mm, "end": v(-59.26, 17.66) * mm});
            skLineSegment(sketch, "E671", {"start": v(-59.26, 17.66) * mm, "end": v(-59.87, 17.5) * mm});
            skLineSegment(sketch, "E672", {"start": v(-59.87, 17.5) * mm, "end": v(-60.49, 17.32) * mm});
            skLineSegment(sketch, "E673", {"start": v(-60.49, 17.32) * mm, "end": v(-61.12, 17.13) * mm});
            skLineSegment(sketch, "E674", {"start": v(-61.12, 17.13) * mm, "end": v(-61.78, 16.91) * mm});
            skLineSegment(sketch, "E675", {"start": v(-61.78, 16.91) * mm, "end": v(-62.44, 16.68) * mm});
            skLineSegment(sketch, "E676", {"start": v(-62.44, 16.68) * mm, "end": v(-63.12, 16.43) * mm});
            skLineSegment(sketch, "E677", {"start": v(-63.12, 16.43) * mm, "end": v(-63.82, 16.15) * mm});
            skLineSegment(sketch, "E678", {"start": v(-63.82, 16.15) * mm, "end": v(-64.23, 15.79) * mm});
            skLineSegment(sketch, "E679", {"start": v(-64.23, 15.79) * mm, "end": v(-64.7, 13.72) * mm});
            skLineSegment(sketch, "E680", {"start": v(-64.7, 13.72) * mm, "end": v(-64.49, 13.21) * mm});
            skLineSegment(sketch, "E681", {"start": v(-64.49, 13.21) * mm, "end": v(-63.98, 12.66) * mm});
            skLineSegment(sketch, "E682", {"start": v(-63.98, 12.66) * mm, "end": v(-63.48, 12.14) * mm});
            skLineSegment(sketch, "E683", {"start": v(-63.48, 12.14) * mm, "end": v(-62.98, 11.64) * mm});
            skLineSegment(sketch, "E684", {"start": v(-62.98, 11.64) * mm, "end": v(-62.49, 11.16) * mm});
            skLineSegment(sketch, "E685", {"start": v(-62.49, 11.16) * mm, "end": v(-62, 10.7) * mm});
            skLineSegment(sketch, "E686", {"start": v(-62, 10.7) * mm, "end": v(-61.52, 10.28) * mm});
            skLineSegment(sketch, "E687", {"start": v(-61.52, 10.28) * mm, "end": v(-61.04, 9.87) * mm});
            skLineSegment(sketch, "E688", {"start": v(-61.04, 9.87) * mm, "end": v(-60.58, 9.48) * mm});
            skLineSegment(sketch, "E689", {"start": v(-60.58, 9.48) * mm, "end": v(-60.12, 9.12) * mm});
            skLineSegment(sketch, "E690", {"start": v(-60.12, 9.12) * mm, "end": v(-59.67, 8.78) * mm});
            skLineSegment(sketch, "E691", {"start": v(-59.67, 8.78) * mm, "end": v(-59.23, 8.45) * mm});
            skLineSegment(sketch, "E692", {"start": v(-59.23, 8.45) * mm, "end": v(-58.8, 8.15) * mm});
            skLineSegment(sketch, "E693", {"start": v(-58.8, 8.15) * mm, "end": v(-58.38, 7.87) * mm});
            skLineSegment(sketch, "E694", {"start": v(-58.38, 7.87) * mm, "end": v(-57.97, 7.6) * mm});
            skLineSegment(sketch, "E695", {"start": v(-57.97, 7.6) * mm, "end": v(-57.57, 7.36) * mm});
            skLineSegment(sketch, "E696", {"start": v(-57.57, 7.36) * mm, "end": v(-57.19, 7.13) * mm});
            skLineSegment(sketch, "E697", {"start": v(-57.19, 7.13) * mm, "end": v(-56.81, 6.92) * mm});
            skLineSegment(sketch, "E698", {"start": v(-56.81, 6.92) * mm, "end": v(-56.46, 6.72) * mm});
            skLineSegment(sketch, "E699", {"start": v(-56.46, 6.72) * mm, "end": v(-56.11, 6.55) * mm});
            skLineSegment(sketch, "E700", {"start": v(-56.11, 6.55) * mm, "end": v(-55.78, 6.38) * mm});
            skLineSegment(sketch, "E701", {"start": v(-55.78, 6.38) * mm, "end": v(-55.47, 6.24) * mm});
            skLineSegment(sketch, "E702", {"start": v(-55.47, 6.24) * mm, "end": v(-55.17, 6.1) * mm});
            skLineSegment(sketch, "E703", {"start": v(-55.17, 6.1) * mm, "end": v(-54.89, 5.98) * mm});
            skLineSegment(sketch, "E704", {"start": v(-54.89, 5.98) * mm, "end": v(-54.62, 5.88) * mm});
            skLineSegment(sketch, "E705", {"start": v(-54.62, 5.88) * mm, "end": v(-54.37, 5.78) * mm});
            skLineSegment(sketch, "E706", {"start": v(-54.37, 5.78) * mm, "end": v(-54.14, 5.7) * mm});
            skLineSegment(sketch, "E707", {"start": v(-54.14, 5.7) * mm, "end": v(-53.92, 5.63) * mm});
            skLineSegment(sketch, "E708", {"start": v(-53.92, 5.63) * mm, "end": v(-53.72, 5.57) * mm});
            skLineSegment(sketch, "E709", {"start": v(-53.72, 5.57) * mm, "end": v(-53.54, 5.51) * mm});
            skLineSegment(sketch, "E710", {"start": v(-53.54, 5.51) * mm, "end": v(-53.38, 5.47) * mm});
            skLineSegment(sketch, "E711", {"start": v(-53.38, 5.47) * mm, "end": v(-53.24, 5.43) * mm});
            skLineSegment(sketch, "E712", {"start": v(-53.24, 5.43) * mm, "end": v(-53.12, 5.4) * mm});
            skLineSegment(sketch, "E713", {"start": v(-53.12, 5.4) * mm, "end": v(-53, 5.38) * mm});
            skLineSegment(sketch, "E714", {"start": v(-53, 5.38) * mm, "end": v(-52.92, 5.37) * mm});
            skLineSegment(sketch, "E715", {"start": v(-52.92, 5.37) * mm, "end": v(-52.86, 5.36) * mm});
            skLineSegment(sketch, "E716", {"start": v(-52.86, 5.36) * mm, "end": v(-52.8, 5.35) * mm});
            skLineSegment(sketch, "E717", {"start": v(-52.8, 5.35) * mm, "end": v(-52.78, 5.35) * mm});
            skLineSegment(sketch, "E718", {"start": v(-52.78, 5.35) * mm, "end": v(-51.66, 5.23) * mm});
            skLineSegment(sketch, "E719", {"start": v(-51.66, 5.23) * mm, "end": v(-51.92, 0) * mm});
            skLineSegment(sketch, "E720", {"start": v(-51.92, 0) * mm, "end": v(-53.05, 0) * mm});
            skLineSegment(sketch, "E721", {"start": v(-53.05, 0) * mm, "end": v(-53.08, 0) * mm});
            skLineSegment(sketch, "E722", {"start": v(-53.08, 0) * mm, "end": v(-53.13, 0) * mm});
            skLineSegment(sketch, "E723", {"start": v(-53.13, 0) * mm, "end": v(-53.2, 0) * mm});
            skLineSegment(sketch, "E724", {"start": v(-53.2, 0) * mm, "end": v(-53.28, -0.02) * mm});
            skLineSegment(sketch, "E725", {"start": v(-53.28, -0.02) * mm, "end": v(-53.39, -0.03) * mm});
            skLineSegment(sketch, "E726", {"start": v(-53.39, -0.03) * mm, "end": v(-53.52, -0.04) * mm});
            skLineSegment(sketch, "E727", {"start": v(-53.52, -0.04) * mm, "end": v(-53.66, -0.06) * mm});
            skLineSegment(sketch, "E728", {"start": v(-53.66, -0.06) * mm, "end": v(-53.83, -0.1) * mm});
            skLineSegment(sketch, "E729", {"start": v(-53.83, -0.1) * mm, "end": v(-54.01, -0.12) * mm});
            skLineSegment(sketch, "E730", {"start": v(-54.01, -0.12) * mm, "end": v(-54.21, -0.17) * mm});
            skLineSegment(sketch, "E731", {"start": v(-54.21, -0.17) * mm, "end": v(-54.44, -0.22) * mm});
            skLineSegment(sketch, "E732", {"start": v(-54.44, -0.22) * mm, "end": v(-54.68, -0.28) * mm});
            skLineSegment(sketch, "E733", {"start": v(-54.68, -0.28) * mm, "end": v(-54.94, -0.34) * mm});
            skLineSegment(sketch, "E734", {"start": v(-54.94, -0.34) * mm, "end": v(-55.21, -0.42) * mm});
            skLineSegment(sketch, "E735", {"start": v(-55.21, -0.42) * mm, "end": v(-55.5, -0.51) * mm});
            skLineSegment(sketch, "E736", {"start": v(-55.5, -0.51) * mm, "end": v(-55.81, -0.62) * mm});
            skLineSegment(sketch, "E737", {"start": v(-55.81, -0.62) * mm, "end": v(-56.14, -0.73) * mm});
            skLineSegment(sketch, "E738", {"start": v(-56.14, -0.73) * mm, "end": v(-56.49, -0.86) * mm});
            skLineSegment(sketch, "E739", {"start": v(-56.49, -0.86) * mm, "end": v(-56.85, -1) * mm});
            skLineSegment(sketch, "E740", {"start": v(-56.85, -1) * mm, "end": v(-57.22, -1.16) * mm});
            skLineSegment(sketch, "E741", {"start": v(-57.22, -1.16) * mm, "end": v(-57.61, -1.33) * mm});
            skLineSegment(sketch, "E742", {"start": v(-57.61, -1.33) * mm, "end": v(-58.02, -1.52) * mm});
            skLineSegment(sketch, "E743", {"start": v(-58.02, -1.52) * mm, "end": v(-58.44, -1.72) * mm});
            skLineSegment(sketch, "E744", {"start": v(-58.44, -1.72) * mm, "end": v(-58.87, -1.94) * mm});
            skLineSegment(sketch, "E745", {"start": v(-58.87, -1.94) * mm, "end": v(-59.32, -2.18) * mm});
            skLineSegment(sketch, "E746", {"start": v(-59.32, -2.18) * mm, "end": v(-59.78, -2.44) * mm});
            skLineSegment(sketch, "E747", {"start": v(-59.78, -2.44) * mm, "end": v(-60.25, -2.72) * mm});
            skLineSegment(sketch, "E748", {"start": v(-60.25, -2.72) * mm, "end": v(-60.73, -3.02) * mm});
            skLineSegment(sketch, "E749", {"start": v(-60.73, -3.02) * mm, "end": v(-61.22, -3.33) * mm});
            skLineSegment(sketch, "E750", {"start": v(-61.22, -3.33) * mm, "end": v(-61.73, -3.67) * mm});
            skLineSegment(sketch, "E751", {"start": v(-61.73, -3.67) * mm, "end": v(-62.24, -4.03) * mm});
            skLineSegment(sketch, "E752", {"start": v(-62.24, -4.03) * mm, "end": v(-62.76, -4.4) * mm});
            skLineSegment(sketch, "E753", {"start": v(-62.76, -4.4) * mm, "end": v(-63.3, -4.8) * mm});
            skLineSegment(sketch, "E754", {"start": v(-63.3, -4.8) * mm, "end": v(-63.83, -5.23) * mm});
            skLineSegment(sketch, "E755", {"start": v(-63.83, -5.23) * mm, "end": v(-64.38, -5.68) * mm});
            skLineSegment(sketch, "E756", {"start": v(-64.38, -5.68) * mm, "end": v(-64.93, -6.15) * mm});
            skLineSegment(sketch, "E757", {"start": v(-64.93, -6.15) * mm, "end": v(-65.5, -6.65) * mm});
            skLineSegment(sketch, "E758", {"start": v(-65.5, -6.65) * mm, "end": v(-65.76, -7.14) * mm});
            skLineSegment(sketch, "E759", {"start": v(-65.76, -7.14) * mm, "end": v(-65.5, -9.23) * mm});
            skLineSegment(sketch, "E760", {"start": v(-65.5, -9.23) * mm, "end": v(-65.12, -9.64) * mm});
            skLineSegment(sketch, "E761", {"start": v(-65.12, -9.64) * mm, "end": v(-64.46, -9.98) * mm});
            skLineSegment(sketch, "E762", {"start": v(-64.46, -9.98) * mm, "end": v(-63.8, -10.3) * mm});
            skLineSegment(sketch, "E763", {"start": v(-63.8, -10.3) * mm, "end": v(-63.17, -10.6) * mm});
            skLineSegment(sketch, "E764", {"start": v(-63.17, -10.6) * mm, "end": v(-62.54, -10.88) * mm});
            skLineSegment(sketch, "E765", {"start": v(-62.54, -10.88) * mm, "end": v(-61.92, -11.14) * mm});
            skLineSegment(sketch, "E766", {"start": v(-61.92, -11.14) * mm, "end": v(-61.32, -11.38) * mm});
            skLineSegment(sketch, "E767", {"start": v(-61.32, -11.38) * mm, "end": v(-60.74, -11.6) * mm});
            skLineSegment(sketch, "E768", {"start": v(-60.74, -11.6) * mm, "end": v(-60.17, -11.8) * mm});
            skLineSegment(sketch, "E769", {"start": v(-60.17, -11.8) * mm, "end": v(-59.61, -12) * mm});
            skLineSegment(sketch, "E770", {"start": v(-59.61, -12) * mm, "end": v(-59.07, -12.16) * mm});
            skLineSegment(sketch, "E771", {"start": v(-59.07, -12.16) * mm, "end": v(-58.54, -12.31) * mm});
            skLineSegment(sketch, "E772", {"start": v(-58.54, -12.31) * mm, "end": v(-58.04, -12.45) * mm});
            skLineSegment(sketch, "E773", {"start": v(-58.04, -12.45) * mm, "end": v(-57.55, -12.57) * mm});
            skLineSegment(sketch, "E774", {"start": v(-57.55, -12.57) * mm, "end": v(-57.07, -12.68) * mm});
            skLineSegment(sketch, "E775", {"start": v(-57.07, -12.68) * mm, "end": v(-56.61, -12.78) * mm});
            skLineSegment(sketch, "E776", {"start": v(-56.61, -12.78) * mm, "end": v(-56.17, -12.86) * mm});
            skLineSegment(sketch, "E777", {"start": v(-56.17, -12.86) * mm, "end": v(-55.75, -12.93) * mm});
            skLineSegment(sketch, "E778", {"start": v(-55.75, -12.93) * mm, "end": v(-55.35, -13) * mm});
            skLineSegment(sketch, "E779", {"start": v(-55.35, -13) * mm, "end": v(-54.97, -13.04) * mm});
            skLineSegment(sketch, "E780", {"start": v(-54.97, -13.04) * mm, "end": v(-54.6, -13.08) * mm});
            skLineSegment(sketch, "E781", {"start": v(-54.6, -13.08) * mm, "end": v(-54.26, -13.11) * mm});
            skLineSegment(sketch, "E782", {"start": v(-54.26, -13.11) * mm, "end": v(-53.93, -13.13) * mm});
            skLineSegment(sketch, "E783", {"start": v(-53.93, -13.13) * mm, "end": v(-53.62, -13.15) * mm});
            skLineSegment(sketch, "E784", {"start": v(-53.62, -13.15) * mm, "end": v(-53.34, -13.16) * mm});
            skLineSegment(sketch, "E785", {"start": v(-53.34, -13.16) * mm, "end": v(-53.07, -13.16) * mm});
            skLineSegment(sketch, "E786", {"start": v(-53.07, -13.16) * mm, "end": v(-52.82, -13.16) * mm});
            skLineSegment(sketch, "E787", {"start": v(-52.82, -13.16) * mm, "end": v(-52.6, -13.15) * mm});
            skLineSegment(sketch, "E788", {"start": v(-52.6, -13.15) * mm, "end": v(-52.39, -13.15) * mm});
            skLineSegment(sketch, "E789", {"start": v(-52.39, -13.15) * mm, "end": v(-52.2, -13.13) * mm});
            skLineSegment(sketch, "E790", {"start": v(-52.2, -13.13) * mm, "end": v(-52.03, -13.12) * mm});
            skLineSegment(sketch, "E791", {"start": v(-52.03, -13.12) * mm, "end": v(-51.89, -13.1) * mm});
            skLineSegment(sketch, "E792", {"start": v(-51.89, -13.1) * mm, "end": v(-51.76, -13.09) * mm});
            skLineSegment(sketch, "E793", {"start": v(-51.76, -13.09) * mm, "end": v(-51.65, -13.07) * mm});
            skLineSegment(sketch, "E794", {"start": v(-51.65, -13.07) * mm, "end": v(-51.57, -13.06) * mm});
            skLineSegment(sketch, "E795", {"start": v(-51.57, -13.06) * mm, "end": v(-51.5, -13.05) * mm});
            skLineSegment(sketch, "E796", {"start": v(-51.5, -13.05) * mm, "end": v(-51.45, -13.04) * mm});
            skLineSegment(sketch, "E797", {"start": v(-51.45, -13.04) * mm, "end": v(-51.43, -13.03) * mm});
            skLineSegment(sketch, "E798", {"start": v(-51.43, -13.03) * mm, "end": v(-50.33, -12.75) * mm});
            skLineSegment(sketch, "E799", {"start": v(-50.33, -12.75) * mm, "end": v(-48.8, -17.76) * mm});
            skLineSegment(sketch, "E800", {"start": v(-48.8, -17.76) * mm, "end": v(-49.85, -18.14) * mm});
            skLineSegment(sketch, "E801", {"start": v(-49.85, -18.14) * mm, "end": v(-49.88, -18.15) * mm});
            skLineSegment(sketch, "E802", {"start": v(-49.88, -18.15) * mm, "end": v(-49.92, -18.17) * mm});
            skLineSegment(sketch, "E803", {"start": v(-49.92, -18.17) * mm, "end": v(-49.98, -18.2) * mm});
            skLineSegment(sketch, "E804", {"start": v(-49.98, -18.2) * mm, "end": v(-50.06, -18.24) * mm});
            skLineSegment(sketch, "E805", {"start": v(-50.06, -18.24) * mm, "end": v(-50.16, -18.29) * mm});
            skLineSegment(sketch, "E806", {"start": v(-50.16, -18.29) * mm, "end": v(-50.27, -18.34) * mm});
            skLineSegment(sketch, "E807", {"start": v(-50.27, -18.34) * mm, "end": v(-50.4, -18.41) * mm});
            skLineSegment(sketch, "E808", {"start": v(-50.4, -18.41) * mm, "end": v(-50.55, -18.5) * mm});
            skLineSegment(sketch, "E809", {"start": v(-50.55, -18.5) * mm, "end": v(-50.71, -18.59) * mm});
            skLineSegment(sketch, "E810", {"start": v(-50.71, -18.59) * mm, "end": v(-50.89, -18.7) * mm});
            skLineSegment(sketch, "E811", {"start": v(-50.89, -18.7) * mm, "end": v(-51.08, -18.82) * mm});
            skLineSegment(sketch, "E812", {"start": v(-51.08, -18.82) * mm, "end": v(-51.29, -18.96) * mm});
            skLineSegment(sketch, "E813", {"start": v(-51.29, -18.96) * mm, "end": v(-51.5, -19.11) * mm});
            skLineSegment(sketch, "E814", {"start": v(-51.5, -19.11) * mm, "end": v(-51.74, -19.28) * mm});
            skLineSegment(sketch, "E815", {"start": v(-51.74, -19.28) * mm, "end": v(-51.98, -19.47) * mm});
            skLineSegment(sketch, "E816", {"start": v(-51.98, -19.47) * mm, "end": v(-52.24, -19.67) * mm});
            skLineSegment(sketch, "E817", {"start": v(-52.24, -19.67) * mm, "end": v(-52.5, -19.89) * mm});
            skLineSegment(sketch, "E818", {"start": v(-52.5, -19.89) * mm, "end": v(-52.79, -20.13) * mm});
            skLineSegment(sketch, "E819", {"start": v(-52.79, -20.13) * mm, "end": v(-53.08, -20.38) * mm});
            skLineSegment(sketch, "E820", {"start": v(-53.08, -20.38) * mm, "end": v(-53.38, -20.66) * mm});
            skLineSegment(sketch, "E821", {"start": v(-53.38, -20.66) * mm, "end": v(-53.68, -20.95) * mm});
            skLineSegment(sketch, "E822", {"start": v(-53.68, -20.95) * mm, "end": v(-54, -21.27) * mm});
            skLineSegment(sketch, "E823", {"start": v(-54, -21.27) * mm, "end": v(-54.32, -21.6) * mm});
            skLineSegment(sketch, "E824", {"start": v(-54.32, -21.6) * mm, "end": v(-54.66, -21.96) * mm});
            skLineSegment(sketch, "E825", {"start": v(-54.66, -21.96) * mm, "end": v(-55, -22.34) * mm});
            skLineSegment(sketch, "E826", {"start": v(-55, -22.34) * mm, "end": v(-55.34, -22.74) * mm});
            skLineSegment(sketch, "E827", {"start": v(-55.34, -22.74) * mm, "end": v(-55.68, -23.16) * mm});
            skLineSegment(sketch, "E828", {"start": v(-55.68, -23.16) * mm, "end": v(-56.04, -23.6) * mm});
            skLineSegment(sketch, "E829", {"start": v(-56.04, -23.6) * mm, "end": v(-56.4, -24.07) * mm});
            skLineSegment(sketch, "E830", {"start": v(-56.4, -24.07) * mm, "end": v(-56.75, -24.56) * mm});
            skLineSegment(sketch, "E831", {"start": v(-56.75, -24.56) * mm, "end": v(-57.1, -25.07) * mm});
            skLineSegment(sketch, "E832", {"start": v(-57.1, -25.07) * mm, "end": v(-57.47, -25.6) * mm});
            skLineSegment(sketch, "E833", {"start": v(-57.47, -25.6) * mm, "end": v(-57.83, -26.17) * mm});
            skLineSegment(sketch, "E834", {"start": v(-57.83, -26.17) * mm, "end": v(-58.2, -26.75) * mm});
            skLineSegment(sketch, "E835", {"start": v(-58.2, -26.75) * mm, "end": v(-58.56, -27.36) * mm});
            skLineSegment(sketch, "E836", {"start": v(-58.56, -27.36) * mm, "end": v(-58.91, -28) * mm});
            skLineSegment(sketch, "E837", {"start": v(-58.91, -28) * mm, "end": v(-59.27, -28.65) * mm});
            skLineSegment(sketch, "E838", {"start": v(-59.27, -28.65) * mm, "end": v(-59.35, -29.2) * mm});
            skLineSegment(sketch, "E839", {"start": v(-59.35, -29.2) * mm, "end": v(-58.39, -31.08) * mm});
            skLineSegment(sketch, "E840", {"start": v(-58.39, -31.08) * mm, "end": v(-57.9, -31.33) * mm});
            skLineSegment(sketch, "E841", {"start": v(-57.9, -31.33) * mm, "end": v(-57.15, -31.43) * mm});
            skLineSegment(sketch, "E842", {"start": v(-57.15, -31.43) * mm, "end": v(-56.43, -31.5) * mm});
            skLineSegment(sketch, "E843", {"start": v(-56.43, -31.5) * mm, "end": v(-55.73, -31.57) * mm});
            skLineSegment(sketch, "E844", {"start": v(-55.73, -31.57) * mm, "end": v(-55.04, -31.62) * mm});
            skLineSegment(sketch, "E845", {"start": v(-55.04, -31.62) * mm, "end": v(-54.38, -31.65) * mm});
            skLineSegment(sketch, "E846", {"start": v(-54.38, -31.65) * mm, "end": v(-53.73, -31.67) * mm});
            skLineSegment(sketch, "E847", {"start": v(-53.73, -31.67) * mm, "end": v(-53.1, -31.68) * mm});
            skLineSegment(sketch, "E848", {"start": v(-53.1, -31.68) * mm, "end": v(-52.5, -31.67) * mm});
            skLineSegment(sketch, "E849", {"start": v(-52.5, -31.67) * mm, "end": v(-51.91, -31.66) * mm});
            skLineSegment(sketch, "E850", {"start": v(-51.91, -31.66) * mm, "end": v(-51.35, -31.63) * mm});
            skLineSegment(sketch, "E851", {"start": v(-51.35, -31.63) * mm, "end": v(-50.8, -31.6) * mm});
            skLineSegment(sketch, "E852", {"start": v(-50.8, -31.6) * mm, "end": v(-50.28, -31.55) * mm});
            skLineSegment(sketch, "E853", {"start": v(-50.28, -31.55) * mm, "end": v(-49.77, -31.5) * mm});
            skLineSegment(sketch, "E854", {"start": v(-49.77, -31.5) * mm, "end": v(-49.3, -31.44) * mm});
            skLineSegment(sketch, "E855", {"start": v(-49.3, -31.44) * mm, "end": v(-48.83, -31.37) * mm});
            skLineSegment(sketch, "E856", {"start": v(-48.83, -31.37) * mm, "end": v(-48.39, -31.3) * mm});
            skLineSegment(sketch, "E857", {"start": v(-48.39, -31.3) * mm, "end": v(-47.97, -31.22) * mm});
            skLineSegment(sketch, "E858", {"start": v(-47.97, -31.22) * mm, "end": v(-47.57, -31.14) * mm});
            skLineSegment(sketch, "E859", {"start": v(-47.57, -31.14) * mm, "end": v(-47.2, -31.05) * mm});
            skLineSegment(sketch, "E860", {"start": v(-47.2, -31.05) * mm, "end": v(-46.84, -30.97) * mm});
            skLineSegment(sketch, "E861", {"start": v(-46.84, -30.97) * mm, "end": v(-46.5, -30.88) * mm});
            skLineSegment(sketch, "E862", {"start": v(-46.5, -30.88) * mm, "end": v(-46.19, -30.79) * mm});
            skLineSegment(sketch, "E863", {"start": v(-46.19, -30.79) * mm, "end": v(-45.9, -30.7) * mm});
            skLineSegment(sketch, "E864", {"start": v(-45.9, -30.7) * mm, "end": v(-45.62, -30.6) * mm});
            skLineSegment(sketch, "E865", {"start": v(-45.62, -30.6) * mm, "end": v(-45.37, -30.52) * mm});
            skLineSegment(sketch, "E866", {"start": v(-45.37, -30.52) * mm, "end": v(-45.13, -30.43) * mm});
            skLineSegment(sketch, "E867", {"start": v(-45.13, -30.43) * mm, "end": v(-44.92, -30.35) * mm});
            skLineSegment(sketch, "E868", {"start": v(-44.92, -30.35) * mm, "end": v(-44.73, -30.27) * mm});
            skLineSegment(sketch, "E869", {"start": v(-44.73, -30.27) * mm, "end": v(-44.56, -30.2) * mm});
            skLineSegment(sketch, "E870", {"start": v(-44.56, -30.2) * mm, "end": v(-44.4, -30.12) * mm});
            skLineSegment(sketch, "E871", {"start": v(-44.4, -30.12) * mm, "end": v(-44.28, -30.06) * mm});
            skLineSegment(sketch, "E872", {"start": v(-44.28, -30.06) * mm, "end": v(-44.16, -30) * mm});
            skLineSegment(sketch, "E873", {"start": v(-44.16, -30) * mm, "end": v(-44.07, -29.95) * mm});
            skLineSegment(sketch, "E874", {"start": v(-44.07, -29.95) * mm, "end": v(-44, -29.9) * mm});
            skLineSegment(sketch, "E875", {"start": v(-44, -29.9) * mm, "end": v(-43.93, -29.87) * mm});
            skLineSegment(sketch, "E876", {"start": v(-43.93, -29.87) * mm, "end": v(-43.9, -29.85) * mm});
            skLineSegment(sketch, "E877", {"start": v(-43.9, -29.85) * mm, "end": v(-43.87, -29.83) * mm});
            skLineSegment(sketch, "E878", {"start": v(-43.87, -29.83) * mm, "end": v(-42.94, -29.2) * mm});
            skLineSegment(sketch, "E879", {"start": v(-42.94, -29.2) * mm, "end": v(-39.78, -33.38) * mm});
            skLineSegment(sketch, "E880", {"start": v(-39.78, -33.38) * mm, "end": v(-40.64, -34.1) * mm});
            skLineSegment(sketch, "E881", {"start": v(-40.64, -34.1) * mm, "end": v(-40.66, -34.12) * mm});
            skLineSegment(sketch, "E882", {"start": v(-40.66, -34.12) * mm, "end": v(-40.7, -34.15) * mm});
            skLineSegment(sketch, "E883", {"start": v(-40.7, -34.15) * mm, "end": v(-40.74, -34.2) * mm});
            skLineSegment(sketch, "E884", {"start": v(-40.74, -34.2) * mm, "end": v(-40.8, -34.26) * mm});
            skLineSegment(sketch, "E885", {"start": v(-40.8, -34.26) * mm, "end": v(-40.88, -34.34) * mm});
            skLineSegment(sketch, "E886", {"start": v(-40.88, -34.34) * mm, "end": v(-40.97, -34.43) * mm});
            skLineSegment(sketch, "E887", {"start": v(-40.97, -34.43) * mm, "end": v(-41.07, -34.54) * mm});
            skLineSegment(sketch, "E888", {"start": v(-41.07, -34.54) * mm, "end": v(-41.18, -34.67) * mm});
            skLineSegment(sketch, "E889", {"start": v(-41.18, -34.67) * mm, "end": v(-41.3, -34.81) * mm});
            skLineSegment(sketch, "E890", {"start": v(-41.3, -34.81) * mm, "end": v(-41.42, -34.98) * mm});
            skLineSegment(sketch, "E891", {"start": v(-41.42, -34.98) * mm, "end": v(-41.56, -35.16) * mm});
            skLineSegment(sketch, "E892", {"start": v(-41.56, -35.16) * mm, "end": v(-41.7, -35.36) * mm});
            skLineSegment(sketch, "E893", {"start": v(-41.7, -35.36) * mm, "end": v(-41.86, -35.58) * mm});
            skLineSegment(sketch, "E894", {"start": v(-41.86, -35.58) * mm, "end": v(-42.02, -35.81) * mm});
            skLineSegment(sketch, "E895", {"start": v(-42.02, -35.81) * mm, "end": v(-42.19, -36.07) * mm});
            skLineSegment(sketch, "E896", {"start": v(-42.19, -36.07) * mm, "end": v(-42.36, -36.35) * mm});
            skLineSegment(sketch, "E897", {"start": v(-42.36, -36.35) * mm, "end": v(-42.54, -36.65) * mm});
            skLineSegment(sketch, "E898", {"start": v(-42.54, -36.65) * mm, "end": v(-42.72, -36.97) * mm});
            skLineSegment(sketch, "E899", {"start": v(-42.72, -36.97) * mm, "end": v(-42.9, -37.3) * mm});
            skLineSegment(sketch, "E900", {"start": v(-42.9, -37.3) * mm, "end": v(-43.09, -37.67) * mm});
            skLineSegment(sketch, "E901", {"start": v(-43.09, -37.67) * mm, "end": v(-43.28, -38.05) * mm});
            skLineSegment(sketch, "E902", {"start": v(-43.28, -38.05) * mm, "end": v(-43.47, -38.46) * mm});
            skLineSegment(sketch, "E903", {"start": v(-43.47, -38.46) * mm, "end": v(-43.66, -38.88) * mm});
            skLineSegment(sketch, "E904", {"start": v(-43.66, -38.88) * mm, "end": v(-43.85, -39.33) * mm});
            skLineSegment(sketch, "E905", {"start": v(-43.85, -39.33) * mm, "end": v(-44.04, -39.8) * mm});
            skLineSegment(sketch, "E906", {"start": v(-44.04, -39.8) * mm, "end": v(-44.22, -40.3) * mm});
            skLineSegment(sketch, "E907", {"start": v(-44.22, -40.3) * mm, "end": v(-44.4, -40.8) * mm});
            skLineSegment(sketch, "E908", {"start": v(-44.4, -40.8) * mm, "end": v(-44.58, -41.35) * mm});
            skLineSegment(sketch, "E909", {"start": v(-44.58, -41.35) * mm, "end": v(-44.76, -41.9) * mm});
            skLineSegment(sketch, "E910", {"start": v(-44.76, -41.9) * mm, "end": v(-44.93, -42.49) * mm});
            skLineSegment(sketch, "E911", {"start": v(-44.93, -42.49) * mm, "end": v(-45.1, -43.1) * mm});
            skLineSegment(sketch, "E912", {"start": v(-45.1, -43.1) * mm, "end": v(-45.25, -43.72) * mm});
            skLineSegment(sketch, "E913", {"start": v(-45.25, -43.72) * mm, "end": v(-45.4, -44.37) * mm});
            skLineSegment(sketch, "E914", {"start": v(-45.4, -44.37) * mm, "end": v(-45.54, -45.04) * mm});
            skLineSegment(sketch, "E915", {"start": v(-45.54, -45.04) * mm, "end": v(-45.67, -45.74) * mm});
            skLineSegment(sketch, "E916", {"start": v(-45.67, -45.74) * mm, "end": v(-45.79, -46.45) * mm});
            skLineSegment(sketch, "E917", {"start": v(-45.79, -46.45) * mm, "end": v(-45.9, -47.19) * mm});
            skLineSegment(sketch, "E918", {"start": v(-45.9, -47.19) * mm, "end": v(-45.79, -47.74) * mm});
            skLineSegment(sketch, "E919", {"start": v(-45.79, -47.74) * mm, "end": v(-44.24, -49.18) * mm});
            skLineSegment(sketch, "E920", {"start": v(-44.24, -49.18) * mm, "end": v(-43.69, -49.24) * mm});
            skLineSegment(sketch, "E921", {"start": v(-43.69, -49.24) * mm, "end": v(-42.96, -49.08) * mm});
            skLineSegment(sketch, "E922", {"start": v(-42.96, -49.08) * mm, "end": v(-42.25, -48.9) * mm});
            skLineSegment(sketch, "E923", {"start": v(-42.25, -48.9) * mm, "end": v(-41.57, -48.72) * mm});
            skLineSegment(sketch, "E924", {"start": v(-41.57, -48.72) * mm, "end": v(-40.91, -48.54) * mm});
            skLineSegment(sketch, "E925", {"start": v(-40.91, -48.54) * mm, "end": v(-40.27, -48.34) * mm});
            skLineSegment(sketch, "E926", {"start": v(-40.27, -48.34) * mm, "end": v(-39.66, -48.14) * mm});
            skLineSegment(sketch, "E927", {"start": v(-39.66, -48.14) * mm, "end": v(-39.07, -47.93) * mm});
            skLineSegment(sketch, "E928", {"start": v(-39.07, -47.93) * mm, "end": v(-38.5, -47.72) * mm});
            skLineSegment(sketch, "E929", {"start": v(-38.5, -47.72) * mm, "end": v(-37.96, -47.5) * mm});
            skLineSegment(sketch, "E930", {"start": v(-37.96, -47.5) * mm, "end": v(-37.43, -47.29) * mm});
            skLineSegment(sketch, "E931", {"start": v(-37.43, -47.29) * mm, "end": v(-36.93, -47.07) * mm});
            skLineSegment(sketch, "E932", {"start": v(-36.93, -47.07) * mm, "end": v(-36.45, -46.84) * mm});
            skLineSegment(sketch, "E933", {"start": v(-36.45, -46.84) * mm, "end": v(-36, -46.62) * mm});
            skLineSegment(sketch, "E934", {"start": v(-36, -46.62) * mm, "end": v(-35.57, -46.4) * mm});
            skLineSegment(sketch, "E935", {"start": v(-35.57, -46.4) * mm, "end": v(-35.15, -46.18) * mm});
            skLineSegment(sketch, "E936", {"start": v(-35.15, -46.18) * mm, "end": v(-34.77, -45.96) * mm});
            skLineSegment(sketch, "E937", {"start": v(-34.77, -45.96) * mm, "end": v(-34.4, -45.74) * mm});
            skLineSegment(sketch, "E938", {"start": v(-34.4, -45.74) * mm, "end": v(-34.05, -45.53) * mm});
            skLineSegment(sketch, "E939", {"start": v(-34.05, -45.53) * mm, "end": v(-33.72, -45.32) * mm});
            skLineSegment(sketch, "E940", {"start": v(-33.72, -45.32) * mm, "end": v(-33.42, -45.12) * mm});
            skLineSegment(sketch, "E941", {"start": v(-33.42, -45.12) * mm, "end": v(-33.13, -44.92) * mm});
            skLineSegment(sketch, "E942", {"start": v(-33.13, -44.92) * mm, "end": v(-32.87, -44.73) * mm});
            skLineSegment(sketch, "E943", {"start": v(-32.87, -44.73) * mm, "end": v(-32.62, -44.54) * mm});
            skLineSegment(sketch, "E944", {"start": v(-32.62, -44.54) * mm, "end": v(-32.4, -44.36) * mm});
            skLineSegment(sketch, "E945", {"start": v(-32.4, -44.36) * mm, "end": v(-32.2, -44.2) * mm});
            skLineSegment(sketch, "E946", {"start": v(-32.2, -44.2) * mm, "end": v(-32, -44.04) * mm});
            skLineSegment(sketch, "E947", {"start": v(-32, -44.04) * mm, "end": v(-31.83, -43.88) * mm});
            skLineSegment(sketch, "E948", {"start": v(-31.83, -43.88) * mm, "end": v(-31.68, -43.74) * mm});
            skLineSegment(sketch, "E949", {"start": v(-31.68, -43.74) * mm, "end": v(-31.55, -43.61) * mm});
            skLineSegment(sketch, "E950", {"start": v(-31.55, -43.61) * mm, "end": v(-31.43, -43.5) * mm});
            skLineSegment(sketch, "E951", {"start": v(-31.43, -43.5) * mm, "end": v(-31.33, -43.39) * mm});
            skLineSegment(sketch, "E952", {"start": v(-31.33, -43.39) * mm, "end": v(-31.24, -43.3) * mm});
            skLineSegment(sketch, "E953", {"start": v(-31.24, -43.3) * mm, "end": v(-31.17, -43.22) * mm});
            skLineSegment(sketch, "E954", {"start": v(-31.17, -43.22) * mm, "end": v(-31.1, -43.15) * mm});
            skLineSegment(sketch, "E955", {"start": v(-31.1, -43.15) * mm, "end": v(-31.07, -43.1) * mm});
            skLineSegment(sketch, "E956", {"start": v(-31.07, -43.1) * mm, "end": v(-31.04, -43.06) * mm});
            skLineSegment(sketch, "E957", {"start": v(-31.04, -43.06) * mm, "end": v(-31.02, -43.04) * mm});
            skLineSegment(sketch, "E958", {"start": v(-31.02, -43.04) * mm, "end": v(-30.36, -42.12) * mm});
            skLineSegment(sketch, "E959", {"start": v(-30.36, -42.12) * mm, "end": v(-25.96, -44.97) * mm});
            skLineSegment(sketch, "E960", {"start": v(-25.96, -44.97) * mm, "end": v(-26.53, -45.94) * mm});
            skLineSegment(sketch, "E961", {"start": v(-26.53, -45.94) * mm, "end": v(-26.54, -45.97) * mm});
            skLineSegment(sketch, "E962", {"start": v(-26.54, -45.97) * mm, "end": v(-26.56, -46.01) * mm});
            skLineSegment(sketch, "E963", {"start": v(-26.56, -46.01) * mm, "end": v(-26.6, -46.07) * mm});
            skLineSegment(sketch, "E964", {"start": v(-26.6, -46.07) * mm, "end": v(-26.63, -46.15) * mm});
            skLineSegment(sketch, "E965", {"start": v(-26.63, -46.15) * mm, "end": v(-26.67, -46.25) * mm});
            skLineSegment(sketch, "E966", {"start": v(-26.67, -46.25) * mm, "end": v(-26.72, -46.37) * mm});
            skLineSegment(sketch, "E967", {"start": v(-26.72, -46.37) * mm, "end": v(-26.78, -46.5) * mm});
            skLineSegment(sketch, "E968", {"start": v(-26.78, -46.5) * mm, "end": v(-26.83, -46.66) * mm});
            skLineSegment(sketch, "E969", {"start": v(-26.83, -46.66) * mm, "end": v(-26.9, -46.84) * mm});
            skLineSegment(sketch, "E970", {"start": v(-26.9, -46.84) * mm, "end": v(-26.96, -47.03) * mm});
            skLineSegment(sketch, "E971", {"start": v(-26.96, -47.03) * mm, "end": v(-27.03, -47.25) * mm});
            skLineSegment(sketch, "E972", {"start": v(-27.03, -47.25) * mm, "end": v(-27.1, -47.49) * mm});
            skLineSegment(sketch, "E973", {"start": v(-27.1, -47.49) * mm, "end": v(-27.17, -47.75) * mm});
            skLineSegment(sketch, "E974", {"start": v(-27.17, -47.75) * mm, "end": v(-27.24, -48.03) * mm});
            skLineSegment(sketch, "E975", {"start": v(-27.24, -48.03) * mm, "end": v(-27.3, -48.33) * mm});
            skLineSegment(sketch, "E976", {"start": v(-27.3, -48.33) * mm, "end": v(-27.37, -48.64) * mm});
            skLineSegment(sketch, "E977", {"start": v(-27.37, -48.64) * mm, "end": v(-27.44, -48.99) * mm});
            skLineSegment(sketch, "E978", {"start": v(-27.44, -48.99) * mm, "end": v(-27.5, -49.35) * mm});
            skLineSegment(sketch, "E979", {"start": v(-27.5, -49.35) * mm, "end": v(-27.56, -49.73) * mm});
            skLineSegment(sketch, "E980", {"start": v(-27.56, -49.73) * mm, "end": v(-27.6, -50.13) * mm});
            skLineSegment(sketch, "E981", {"start": v(-27.6, -50.13) * mm, "end": v(-27.65, -50.56) * mm});
            skLineSegment(sketch, "E982", {"start": v(-27.65, -50.56) * mm, "end": v(-27.7, -51) * mm});
            skLineSegment(sketch, "E983", {"start": v(-27.7, -51) * mm, "end": v(-27.73, -51.47) * mm});
            skLineSegment(sketch, "E984", {"start": v(-27.73, -51.47) * mm, "end": v(-27.75, -51.96) * mm});
            skLineSegment(sketch, "E985", {"start": v(-27.75, -51.96) * mm, "end": v(-27.77, -52.46) * mm});
            skLineSegment(sketch, "E986", {"start": v(-27.77, -52.46) * mm, "end": v(-27.77, -52.99) * mm});
            skLineSegment(sketch, "E987", {"start": v(-27.77, -52.99) * mm, "end": v(-27.77, -53.54) * mm});
            skLineSegment(sketch, "E988", {"start": v(-27.77, -53.54) * mm, "end": v(-27.75, -54.1) * mm});
            skLineSegment(sketch, "E989", {"start": v(-27.75, -54.1) * mm, "end": v(-27.73, -54.69) * mm});
            skLineSegment(sketch, "E990", {"start": v(-27.73, -54.69) * mm, "end": v(-27.69, -55.3) * mm});
            skLineSegment(sketch, "E991", {"start": v(-27.69, -55.3) * mm, "end": v(-27.63, -55.92) * mm});
            skLineSegment(sketch, "E992", {"start": v(-27.63, -55.92) * mm, "end": v(-27.56, -56.56) * mm});
            skLineSegment(sketch, "E993", {"start": v(-27.56, -56.56) * mm, "end": v(-27.48, -57.22) * mm});
            skLineSegment(sketch, "E994", {"start": v(-27.48, -57.22) * mm, "end": v(-27.38, -57.9) * mm});
            skLineSegment(sketch, "E995", {"start": v(-27.38, -57.9) * mm, "end": v(-27.27, -58.6) * mm});
            skLineSegment(sketch, "E996", {"start": v(-27.27, -58.6) * mm, "end": v(-27.14, -59.31) * mm});
            skLineSegment(sketch, "E997", {"start": v(-27.14, -59.31) * mm, "end": v(-26.99, -60.04) * mm});
            skLineSegment(sketch, "E998", {"start": v(-26.99, -60.04) * mm, "end": v(-26.7, -60.52) * mm});
            skLineSegment(sketch, "E999", {"start": v(-26.7, -60.52) * mm, "end": v(-24.75, -61.34) * mm});
            skLineSegment(sketch, "E1000", {"start": v(-24.75, -61.34) * mm, "end": v(-24.2, -61.22) * mm});
            skLineSegment(sketch, "E1001", {"start": v(-24.2, -61.22) * mm, "end": v(-23.58, -60.81) * mm});
            skLineSegment(sketch, "E1002", {"start": v(-23.58, -60.81) * mm, "end": v(-22.98, -60.4) * mm});
            skLineSegment(sketch, "E1003", {"start": v(-22.98, -60.4) * mm, "end": v(-22.4, -60) * mm});
            skLineSegment(sketch, "E1004", {"start": v(-22.4, -60) * mm, "end": v(-21.84, -59.6) * mm});
            skLineSegment(sketch, "E1005", {"start": v(-21.84, -59.6) * mm, "end": v(-21.31, -59.2) * mm});
            skLineSegment(sketch, "E1006", {"start": v(-21.31, -59.2) * mm, "end": v(-20.8, -58.8) * mm});
            skLineSegment(sketch, "E1007", {"start": v(-20.8, -58.8) * mm, "end": v(-20.32, -58.4) * mm});
            skLineSegment(sketch, "E1008", {"start": v(-20.32, -58.4) * mm, "end": v(-19.86, -58) * mm});
            skLineSegment(sketch, "E1009", {"start": v(-19.86, -58) * mm, "end": v(-19.42, -57.62) * mm});
            skLineSegment(sketch, "E1010", {"start": v(-19.42, -57.62) * mm, "end": v(-19, -57.24) * mm});
            skLineSegment(sketch, "E1011", {"start": v(-19, -57.24) * mm, "end": v(-18.6, -56.86) * mm});
            skLineSegment(sketch, "E1012", {"start": v(-18.6, -56.86) * mm, "end": v(-18.24, -56.49) * mm});
            skLineSegment(sketch, "E1013", {"start": v(-18.24, -56.49) * mm, "end": v(-17.88, -56.12) * mm});
            skLineSegment(sketch, "E1014", {"start": v(-17.88, -56.12) * mm, "end": v(-17.55, -55.77) * mm});
            skLineSegment(sketch, "E1015", {"start": v(-17.55, -55.77) * mm, "end": v(-17.24, -55.42) * mm});
            skLineSegment(sketch, "E1016", {"start": v(-17.24, -55.42) * mm, "end": v(-16.95, -55.08) * mm});
            skLineSegment(sketch, "E1017", {"start": v(-16.95, -55.08) * mm, "end": v(-16.68, -54.75) * mm});
            skLineSegment(sketch, "E1018", {"start": v(-16.68, -54.75) * mm, "end": v(-16.43, -54.43) * mm});
            skLineSegment(sketch, "E1019", {"start": v(-16.43, -54.43) * mm, "end": v(-16.19, -54.12) * mm});
            skLineSegment(sketch, "E1020", {"start": v(-16.19, -54.12) * mm, "end": v(-15.97, -53.83) * mm});
            skLineSegment(sketch, "E1021", {"start": v(-15.97, -53.83) * mm, "end": v(-15.77, -53.54) * mm});
            skLineSegment(sketch, "E1022", {"start": v(-15.77, -53.54) * mm, "end": v(-15.59, -53.27) * mm});
            skLineSegment(sketch, "E1023", {"start": v(-15.59, -53.27) * mm, "end": v(-15.42, -53.01) * mm});
            skLineSegment(sketch, "E1024", {"start": v(-15.42, -53.01) * mm, "end": v(-15.27, -52.77) * mm});
            skLineSegment(sketch, "E1025", {"start": v(-15.27, -52.77) * mm, "end": v(-15.14, -52.54) * mm});
            skLineSegment(sketch, "E1026", {"start": v(-15.14, -52.54) * mm, "end": v(-15.01, -52.33) * mm});
            skLineSegment(sketch, "E1027", {"start": v(-15.01, -52.33) * mm, "end": v(-14.9, -52.13) * mm});
            skLineSegment(sketch, "E1028", {"start": v(-14.9, -52.13) * mm, "end": v(-14.8, -51.94) * mm});
            skLineSegment(sketch, "E1029", {"start": v(-14.8, -51.94) * mm, "end": v(-14.73, -51.77) * mm});
            skLineSegment(sketch, "E1030", {"start": v(-14.73, -51.77) * mm, "end": v(-14.66, -51.62) * mm});
            skLineSegment(sketch, "E1031", {"start": v(-14.66, -51.62) * mm, "end": v(-14.6, -51.49) * mm});
            skLineSegment(sketch, "E1032", {"start": v(-14.6, -51.49) * mm, "end": v(-14.55, -51.37) * mm});
            skLineSegment(sketch, "E1033", {"start": v(-14.55, -51.37) * mm, "end": v(-14.5, -51.27) * mm});
            skLineSegment(sketch, "E1034", {"start": v(-14.5, -51.27) * mm, "end": v(-14.47, -51.19) * mm});
            skLineSegment(sketch, "E1035", {"start": v(-14.47, -51.19) * mm, "end": v(-14.45, -51.12) * mm});
            skLineSegment(sketch, "E1036", {"start": v(-14.45, -51.12) * mm, "end": v(-14.44, -51.08) * mm});
            skLineSegment(sketch, "E1037", {"start": v(-14.44, -51.08) * mm, "end": v(-14.43, -51.05) * mm});
            skLineSegment(sketch, "E1038", {"start": v(-14.43, -51.05) * mm, "end": v(-14.12, -49.97) * mm});
            skLineSegment(sketch, "E1039", {"start": v(-14.12, -49.97) * mm, "end": v(-9.02, -51.14) * mm});
            skLineSegment(sketch, "E1040", {"start": v(-9.02, -51.14) * mm, "end": v(-9.21, -52.24) * mm});
            skLineSegment(sketch, "E1041", {"start": v(-9.21, -52.24) * mm, "end": v(-9.22, -52.27) * mm});
            skLineSegment(sketch, "E1042", {"start": v(-9.22, -52.27) * mm, "end": v(-9.22, -52.32) * mm});
            skLineSegment(sketch, "E1043", {"start": v(-9.22, -52.32) * mm, "end": v(-9.23, -52.39) * mm});
            skLineSegment(sketch, "E1044", {"start": v(-9.23, -52.39) * mm, "end": v(-9.24, -52.47) * mm});
            skLineSegment(sketch, "E1045", {"start": v(-9.24, -52.47) * mm, "end": v(-9.25, -52.58) * mm});
            skLineSegment(sketch, "E1046", {"start": v(-9.25, -52.58) * mm, "end": v(-9.25, -52.71) * mm});
            skLineSegment(sketch, "E1047", {"start": v(-9.25, -52.71) * mm, "end": v(-9.26, -52.86) * mm});
            skLineSegment(sketch, "E1048", {"start": v(-9.26, -52.86) * mm, "end": v(-9.26, -53.03) * mm});
            skLineSegment(sketch, "E1049", {"start": v(-9.26, -53.03) * mm, "end": v(-9.26, -53.21) * mm});
            skLineSegment(sketch, "E1050", {"start": v(-9.26, -53.21) * mm, "end": v(-9.25, -53.42) * mm});
            skLineSegment(sketch, "E1051", {"start": v(-9.25, -53.42) * mm, "end": v(-9.24, -53.65) * mm});
            skLineSegment(sketch, "E1052", {"start": v(-9.24, -53.65) * mm, "end": v(-9.22, -53.9) * mm});
            skLineSegment(sketch, "E1053", {"start": v(-9.22, -53.9) * mm, "end": v(-9.2, -54.16) * mm});
            skLineSegment(sketch, "E1054", {"start": v(-9.2, -54.16) * mm, "end": v(-9.17, -54.45) * mm});
            skLineSegment(sketch, "E1055", {"start": v(-9.17, -54.45) * mm, "end": v(-9.13, -54.75) * mm});
            skLineSegment(sketch, "E1056", {"start": v(-9.13, -54.75) * mm, "end": v(-9.09, -55.07) * mm});
            skLineSegment(sketch, "E1057", {"start": v(-9.09, -55.07) * mm, "end": v(-9.03, -55.42) * mm});
            skLineSegment(sketch, "E1058", {"start": v(-9.03, -55.42) * mm, "end": v(-8.96, -55.78) * mm});
            skLineSegment(sketch, "E1059", {"start": v(-8.96, -55.78) * mm, "end": v(-8.89, -56.16) * mm});
            skLineSegment(sketch, "E1060", {"start": v(-8.89, -56.16) * mm, "end": v(-8.8, -56.55) * mm});
            skLineSegment(sketch, "E1061", {"start": v(-8.8, -56.55) * mm, "end": v(-8.7, -56.97) * mm});
            skLineSegment(sketch, "E1062", {"start": v(-8.7, -56.97) * mm, "end": v(-8.58, -57.4) * mm});
            skLineSegment(sketch, "E1063", {"start": v(-8.58, -57.4) * mm, "end": v(-8.45, -57.85) * mm});
            skLineSegment(sketch, "E1064", {"start": v(-8.45, -57.85) * mm, "end": v(-8.3, -58.31) * mm});
            skLineSegment(sketch, "E1065", {"start": v(-8.3, -58.31) * mm, "end": v(-8.15, -58.8) * mm});
            skLineSegment(sketch, "E1066", {"start": v(-8.15, -58.8) * mm, "end": v(-7.97, -59.3) * mm});
            skLineSegment(sketch, "E1067", {"start": v(-7.97, -59.3) * mm, "end": v(-7.78, -59.8) * mm});
            skLineSegment(sketch, "E1068", {"start": v(-7.78, -59.8) * mm, "end": v(-7.58, -60.33) * mm});
            skLineSegment(sketch, "E1069", {"start": v(-7.58, -60.33) * mm, "end": v(-7.35, -60.87) * mm});
            skLineSegment(sketch, "E1070", {"start": v(-7.35, -60.87) * mm, "end": v(-7.1, -61.43) * mm});
            skLineSegment(sketch, "E1071", {"start": v(-7.1, -61.43) * mm, "end": v(-6.84, -62) * mm});
            skLineSegment(sketch, "E1072", {"start": v(-6.84, -62) * mm, "end": v(-6.56, -62.58) * mm});
            skLineSegment(sketch, "E1073", {"start": v(-6.56, -62.58) * mm, "end": v(-6.25, -63.17) * mm});
            skLineSegment(sketch, "E1074", {"start": v(-6.25, -63.17) * mm, "end": v(-5.93, -63.77) * mm});
            skLineSegment(sketch, "E1075", {"start": v(-5.93, -63.77) * mm, "end": v(-5.58, -64.4) * mm});
            skLineSegment(sketch, "E1076", {"start": v(-5.58, -64.4) * mm, "end": v(-5.22, -65.02) * mm});
            skLineSegment(sketch, "E1077", {"start": v(-5.22, -65.02) * mm, "end": v(-4.83, -65.65) * mm});
            skLineSegment(sketch, "E1078", {"start": v(-4.83, -65.65) * mm, "end": v(-4.4, -66) * mm});
            skLineSegment(sketch, "E1079", {"start": v(-4.4, -66) * mm, "end": v(-2.28, -66.1) * mm});
            skLineSegment(sketch, "E1080", {"start": v(-2.28, -66.1) * mm, "end": v(-1.81, -65.8) * mm});
            skLineSegment(sketch, "E1081", {"start": v(-1.81, -65.8) * mm, "end": v(-1.36, -65.21) * mm});
            skLineSegment(sketch, "E1082", {"start": v(-1.36, -65.21) * mm, "end": v(-0.93, -64.62) * mm});
            skLineSegment(sketch, "E1083", {"start": v(-0.93, -64.62) * mm, "end": v(-0.52, -64.05) * mm});
            skLineSegment(sketch, "E1084", {"start": v(-0.52, -64.05) * mm, "end": v(-0.14, -63.48) * mm});
            skLineSegment(sketch, "E1085", {"start": v(-0.14, -63.48) * mm, "end": v(0.22, -62.92) * mm});
            skLineSegment(sketch, "E1086", {"start": v(0.22, -62.92) * mm, "end": v(0.56, -62.37) * mm});
            skLineSegment(sketch, "E1087", {"start": v(0.56, -62.37) * mm, "end": v(0.88, -61.83) * mm});
            skLineSegment(sketch, "E1088", {"start": v(0.88, -61.83) * mm, "end": v(1.18, -61.3) * mm});
            skLineSegment(sketch, "E1089", {"start": v(1.18, -61.3) * mm, "end": v(1.46, -60.79) * mm});
            skLineSegment(sketch, "E1090", {"start": v(1.46, -60.79) * mm, "end": v(1.72, -60.28) * mm});
            skLineSegment(sketch, "E1091", {"start": v(1.72, -60.28) * mm, "end": v(1.96, -59.8) * mm});
            skLineSegment(sketch, "E1092", {"start": v(1.96, -59.8) * mm, "end": v(2.18, -59.32) * mm});
            skLineSegment(sketch, "E1093", {"start": v(2.18, -59.32) * mm, "end": v(2.4, -58.85) * mm});
            skLineSegment(sketch, "E1094", {"start": v(2.4, -58.85) * mm, "end": v(2.58, -58.4) * mm});
            skLineSegment(sketch, "E1095", {"start": v(2.58, -58.4) * mm, "end": v(2.75, -57.97) * mm});
            skLineSegment(sketch, "E1096", {"start": v(2.75, -57.97) * mm, "end": v(2.91, -57.56) * mm});
            skLineSegment(sketch, "E1097", {"start": v(2.91, -57.56) * mm, "end": v(3.05, -57.15) * mm});
            skLineSegment(sketch, "E1098", {"start": v(3.05, -57.15) * mm, "end": v(3.18, -56.77) * mm});
            skLineSegment(sketch, "E1099", {"start": v(3.18, -56.77) * mm, "end": v(3.3, -56.4) * mm});
            skLineSegment(sketch, "E1100", {"start": v(3.3, -56.4) * mm, "end": v(3.4, -56.04) * mm});
            skLineSegment(sketch, "E1101", {"start": v(3.4, -56.04) * mm, "end": v(3.5, -55.71) * mm});
            skLineSegment(sketch, "E1102", {"start": v(3.5, -55.71) * mm, "end": v(3.57, -55.4) * mm});
            skLineSegment(sketch, "E1103", {"start": v(3.57, -55.4) * mm, "end": v(3.64, -55.1) * mm});
            skLineSegment(sketch, "E1104", {"start": v(3.64, -55.1) * mm, "end": v(3.7, -54.81) * mm});
            skLineSegment(sketch, "E1105", {"start": v(3.7, -54.81) * mm, "end": v(3.75, -54.55) * mm});
            skLineSegment(sketch, "E1106", {"start": v(3.75, -54.55) * mm, "end": v(3.79, -54.3) * mm});
            skLineSegment(sketch, "E1107", {"start": v(3.79, -54.3) * mm, "end": v(3.82, -54.08) * mm});
            skLineSegment(sketch, "E1108", {"start": v(3.82, -54.08) * mm, "end": v(3.85, -53.87) * mm});
            skLineSegment(sketch, "E1109", {"start": v(3.85, -53.87) * mm, "end": v(3.87, -53.69) * mm});
            skLineSegment(sketch, "E1110", {"start": v(3.87, -53.69) * mm, "end": v(3.88, -53.52) * mm});
            skLineSegment(sketch, "E1111", {"start": v(3.88, -53.52) * mm, "end": v(3.9, -53.37) * mm});
            skLineSegment(sketch, "E1112", {"start": v(3.9, -53.37) * mm, "end": v(3.9, -53.25) * mm});
            skLineSegment(sketch, "E1113", {"start": v(3.9, -53.25) * mm, "end": v(3.9, -53.14) * mm});
            skLineSegment(sketch, "E1114", {"start": v(3.9, -53.14) * mm, "end": v(3.9, -53.05) * mm});
            skLineSegment(sketch, "E1115", {"start": v(3.9, -53.05) * mm, "end": v(3.9, -52.98) * mm});
            skLineSegment(sketch, "E1116", {"start": v(3.9, -52.98) * mm, "end": v(3.9, -52.93) * mm});
            skLineSegment(sketch, "E1117", {"start": v(3.9, -52.93) * mm, "end": v(3.9, -52.9) * mm});
            skLineSegment(sketch, "E1118", {"start": v(3.9, -52.9) * mm, "end": v(3.82, -51.78) * mm});
            skLineSegment(sketch, "E1119", {"start": v(3.82, -51.78) * mm, "end": v(9.02, -51.14) * mm});
            skLineSegment(sketch, "E1120", {"start": v(9.02, -51.14) * mm, "end": v(9.21, -52.24) * mm});
            skLineSegment(sketch, "E1121", {"start": v(9.21, -52.24) * mm, "end": v(9.22, -52.27) * mm});
            skLineSegment(sketch, "E1122", {"start": v(9.22, -52.27) * mm, "end": v(9.23, -52.32) * mm});
            skLineSegment(sketch, "E1123", {"start": v(9.23, -52.32) * mm, "end": v(9.25, -52.38) * mm});
            skLineSegment(sketch, "E1124", {"start": v(9.25, -52.38) * mm, "end": v(9.27, -52.47) * mm});
            skLineSegment(sketch, "E1125", {"start": v(9.27, -52.47) * mm, "end": v(9.3, -52.57) * mm});
            skLineSegment(sketch, "E1126", {"start": v(9.3, -52.57) * mm, "end": v(9.33, -52.7) * mm});
            skLineSegment(sketch, "E1127", {"start": v(9.33, -52.7) * mm, "end": v(9.38, -52.84) * mm});
            skLineSegment(sketch, "E1128", {"start": v(9.38, -52.84) * mm, "end": v(9.44, -53) * mm});
            skLineSegment(sketch, "E1129", {"start": v(9.44, -53) * mm, "end": v(9.5, -53.17) * mm});
            skLineSegment(sketch, "E1130", {"start": v(9.5, -53.17) * mm, "end": v(9.58, -53.36) * mm});
            skLineSegment(sketch, "E1131", {"start": v(9.58, -53.36) * mm, "end": v(9.67, -53.57) * mm});
            skLineSegment(sketch, "E1132", {"start": v(9.67, -53.57) * mm, "end": v(9.76, -53.8) * mm});
            skLineSegment(sketch, "E1133", {"start": v(9.76, -53.8) * mm, "end": v(9.88, -54.04) * mm});
            skLineSegment(sketch, "E1134", {"start": v(9.88, -54.04) * mm, "end": v(10, -54.3) * mm});
            skLineSegment(sketch, "E1135", {"start": v(10, -54.3) * mm, "end": v(10.14, -54.57) * mm});
            skLineSegment(sketch, "E1136", {"start": v(10.14, -54.57) * mm, "end": v(10.3, -54.86) * mm});
            skLineSegment(sketch, "E1137", {"start": v(10.3, -54.86) * mm, "end": v(10.47, -55.16) * mm});
            skLineSegment(sketch, "E1138", {"start": v(10.47, -55.16) * mm, "end": v(10.65, -55.48) * mm});
            skLineSegment(sketch, "E1139", {"start": v(10.65, -55.48) * mm, "end": v(10.86, -55.8) * mm});
            skLineSegment(sketch, "E1140", {"start": v(10.86, -55.8) * mm, "end": v(11.08, -56.15) * mm});
            skLineSegment(sketch, "E1141", {"start": v(11.08, -56.15) * mm, "end": v(11.31, -56.5) * mm});
            skLineSegment(sketch, "E1142", {"start": v(11.31, -56.5) * mm, "end": v(11.57, -56.87) * mm});
            skLineSegment(sketch, "E1143", {"start": v(11.57, -56.87) * mm, "end": v(11.84, -57.25) * mm});
            skLineSegment(sketch, "E1144", {"start": v(11.84, -57.25) * mm, "end": v(12.14, -57.64) * mm});
            skLineSegment(sketch, "E1145", {"start": v(12.14, -57.64) * mm, "end": v(12.45, -58.04) * mm});
            skLineSegment(sketch, "E1146", {"start": v(12.45, -58.04) * mm, "end": v(12.79, -58.44) * mm});
            skLineSegment(sketch, "E1147", {"start": v(12.79, -58.44) * mm, "end": v(13.14, -58.86) * mm});
            skLineSegment(sketch, "E1148", {"start": v(13.14, -58.86) * mm, "end": v(13.52, -59.28) * mm});
            skLineSegment(sketch, "E1149", {"start": v(13.52, -59.28) * mm, "end": v(13.91, -59.71) * mm});
            skLineSegment(sketch, "E1150", {"start": v(13.91, -59.71) * mm, "end": v(14.33, -60.15) * mm});
            skLineSegment(sketch, "E1151", {"start": v(14.33, -60.15) * mm, "end": v(14.78, -60.6) * mm});
            skLineSegment(sketch, "E1152", {"start": v(14.78, -60.6) * mm, "end": v(15.24, -61.05) * mm});
            skLineSegment(sketch, "E1153", {"start": v(15.24, -61.05) * mm, "end": v(15.73, -61.5) * mm});
            skLineSegment(sketch, "E1154", {"start": v(15.73, -61.5) * mm, "end": v(16.24, -61.96) * mm});
            skLineSegment(sketch, "E1155", {"start": v(16.24, -61.96) * mm, "end": v(16.78, -62.42) * mm});
            skLineSegment(sketch, "E1156", {"start": v(16.78, -62.42) * mm, "end": v(17.34, -62.88) * mm});
            skLineSegment(sketch, "E1157", {"start": v(17.34, -62.88) * mm, "end": v(17.92, -63.34) * mm});
            skLineSegment(sketch, "E1158", {"start": v(17.92, -63.34) * mm, "end": v(18.45, -63.52) * mm});
            skLineSegment(sketch, "E1159", {"start": v(18.45, -63.52) * mm, "end": v(20.47, -62.9) * mm});
            skLineSegment(sketch, "E1160", {"start": v(20.47, -62.9) * mm, "end": v(20.8, -62.46) * mm});
            skLineSegment(sketch, "E1161", {"start": v(20.8, -62.46) * mm, "end": v(21.02, -61.74) * mm});
            skLineSegment(sketch, "E1162", {"start": v(21.02, -61.74) * mm, "end": v(21.23, -61.05) * mm});
            skLineSegment(sketch, "E1163", {"start": v(21.23, -61.05) * mm, "end": v(21.41, -60.36) * mm});
            skLineSegment(sketch, "E1164", {"start": v(21.41, -60.36) * mm, "end": v(21.58, -59.7) * mm});
            skLineSegment(sketch, "E1165", {"start": v(21.58, -59.7) * mm, "end": v(21.73, -59.05) * mm});
            skLineSegment(sketch, "E1166", {"start": v(21.73, -59.05) * mm, "end": v(21.86, -58.42) * mm});
            skLineSegment(sketch, "E1167", {"start": v(21.86, -58.42) * mm, "end": v(21.97, -57.8) * mm});
            skLineSegment(sketch, "E1168", {"start": v(21.97, -57.8) * mm, "end": v(22.07, -57.2) * mm});
            skLineSegment(sketch, "E1169", {"start": v(22.07, -57.2) * mm, "end": v(22.16, -56.62) * mm});
            skLineSegment(sketch, "E1170", {"start": v(22.16, -56.62) * mm, "end": v(22.23, -56.06) * mm});
            skLineSegment(sketch, "E1171", {"start": v(22.23, -56.06) * mm, "end": v(22.3, -55.52) * mm});
            skLineSegment(sketch, "E1172", {"start": v(22.3, -55.52) * mm, "end": v(22.34, -55) * mm});
            skLineSegment(sketch, "E1173", {"start": v(22.34, -55) * mm, "end": v(22.38, -54.49) * mm});
            skLineSegment(sketch, "E1174", {"start": v(22.38, -54.49) * mm, "end": v(22.4, -54) * mm});
            skLineSegment(sketch, "E1175", {"start": v(22.4, -54) * mm, "end": v(22.42, -53.54) * mm});
            skLineSegment(sketch, "E1176", {"start": v(22.42, -53.54) * mm, "end": v(22.42, -53.09) * mm});
            skLineSegment(sketch, "E1177", {"start": v(22.42, -53.09) * mm, "end": v(22.42, -52.66) * mm});
            skLineSegment(sketch, "E1178", {"start": v(22.42, -52.66) * mm, "end": v(22.4, -52.25) * mm});
            skLineSegment(sketch, "E1179", {"start": v(22.4, -52.25) * mm, "end": v(22.39, -51.87) * mm});
            skLineSegment(sketch, "E1180", {"start": v(22.39, -51.87) * mm, "end": v(22.36, -51.5) * mm});
            skLineSegment(sketch, "E1181", {"start": v(22.36, -51.5) * mm, "end": v(22.33, -51.16) * mm});
            skLineSegment(sketch, "E1182", {"start": v(22.33, -51.16) * mm, "end": v(22.3, -50.83) * mm});
            skLineSegment(sketch, "E1183", {"start": v(22.3, -50.83) * mm, "end": v(22.26, -50.53) * mm});
            skLineSegment(sketch, "E1184", {"start": v(22.26, -50.53) * mm, "end": v(22.22, -50.24) * mm});
            skLineSegment(sketch, "E1185", {"start": v(22.22, -50.24) * mm, "end": v(22.18, -49.98) * mm});
            skLineSegment(sketch, "E1186", {"start": v(22.18, -49.98) * mm, "end": v(22.13, -49.73) * mm});
            skLineSegment(sketch, "E1187", {"start": v(22.13, -49.73) * mm, "end": v(22.09, -49.51) * mm});
            skLineSegment(sketch, "E1188", {"start": v(22.09, -49.51) * mm, "end": v(22.04, -49.3) * mm});
            skLineSegment(sketch, "E1189", {"start": v(22.04, -49.3) * mm, "end": v(22, -49.13) * mm});
            skLineSegment(sketch, "E1190", {"start": v(22, -49.13) * mm, "end": v(21.95, -48.96) * mm});
            skLineSegment(sketch, "E1191", {"start": v(21.95, -48.96) * mm, "end": v(21.91, -48.82) * mm});
            skLineSegment(sketch, "E1192", {"start": v(21.91, -48.82) * mm, "end": v(21.88, -48.7) * mm});
            skLineSegment(sketch, "E1193", {"start": v(21.88, -48.7) * mm, "end": v(21.84, -48.6) * mm});
            skLineSegment(sketch, "E1194", {"start": v(21.84, -48.6) * mm, "end": v(21.81, -48.52) * mm});
            skLineSegment(sketch, "E1195", {"start": v(21.81, -48.52) * mm, "end": v(21.79, -48.45) * mm});
            skLineSegment(sketch, "E1196", {"start": v(21.79, -48.45) * mm, "end": v(21.77, -48.4) * mm});
            skLineSegment(sketch, "E1197", {"start": v(21.77, -48.4) * mm, "end": v(21.76, -48.38) * mm});
            skLineSegment(sketch, "E1198", {"start": v(21.76, -48.38) * mm, "end": v(21.3, -47.35) * mm});
            skLineSegment(sketch, "E1199", {"start": v(21.3, -47.35) * mm, "end": v(25.96, -44.97) * mm});
            skLineSegment(sketch, "E1200", {"start": v(25.96, -44.97) * mm, "end": v(26.53, -45.94) * mm});
            skLineSegment(sketch, "E1201", {"start": v(26.53, -45.94) * mm, "end": v(26.54, -45.97) * mm});
            skLineSegment(sketch, "E1202", {"start": v(26.54, -45.97) * mm, "end": v(26.57, -46) * mm});
            skLineSegment(sketch, "E1203", {"start": v(26.57, -46) * mm, "end": v(26.6, -46.06) * mm});
            skLineSegment(sketch, "E1204", {"start": v(26.6, -46.06) * mm, "end": v(26.65, -46.14) * mm});
            skLineSegment(sketch, "E1205", {"start": v(26.65, -46.14) * mm, "end": v(26.72, -46.22) * mm});
            skLineSegment(sketch, "E1206", {"start": v(26.72, -46.22) * mm, "end": v(26.8, -46.32) * mm});
            skLineSegment(sketch, "E1207", {"start": v(26.8, -46.32) * mm, "end": v(26.89, -46.44) * mm});
            skLineSegment(sketch, "E1208", {"start": v(26.89, -46.44) * mm, "end": v(27, -46.57) * mm});
            skLineSegment(sketch, "E1209", {"start": v(27, -46.57) * mm, "end": v(27.11, -46.71) * mm});
            skLineSegment(sketch, "E1210", {"start": v(27.11, -46.71) * mm, "end": v(27.25, -46.87) * mm});
            skLineSegment(sketch, "E1211", {"start": v(27.25, -46.87) * mm, "end": v(27.4, -47.04) * mm});
            skLineSegment(sketch, "E1212", {"start": v(27.4, -47.04) * mm, "end": v(27.58, -47.21) * mm});
            skLineSegment(sketch, "E1213", {"start": v(27.58, -47.21) * mm, "end": v(27.76, -47.4) * mm});
            skLineSegment(sketch, "E1214", {"start": v(27.76, -47.4) * mm, "end": v(27.97, -47.6) * mm});
            skLineSegment(sketch, "E1215", {"start": v(27.97, -47.6) * mm, "end": v(28.2, -47.81) * mm});
            skLineSegment(sketch, "E1216", {"start": v(28.2, -47.81) * mm, "end": v(28.44, -48.03) * mm});
            skLineSegment(sketch, "E1217", {"start": v(28.44, -48.03) * mm, "end": v(28.7, -48.26) * mm});
            skLineSegment(sketch, "E1218", {"start": v(28.7, -48.26) * mm, "end": v(28.99, -48.49) * mm});
            skLineSegment(sketch, "E1219", {"start": v(28.99, -48.49) * mm, "end": v(29.3, -48.73) * mm});
            skLineSegment(sketch, "E1220", {"start": v(29.3, -48.73) * mm, "end": v(29.61, -48.98) * mm});
            skLineSegment(sketch, "E1221", {"start": v(29.61, -48.98) * mm, "end": v(29.96, -49.23) * mm});
            skLineSegment(sketch, "E1222", {"start": v(29.96, -49.23) * mm, "end": v(30.32, -49.49) * mm});
            skLineSegment(sketch, "E1223", {"start": v(30.32, -49.49) * mm, "end": v(30.71, -49.75) * mm});
            skLineSegment(sketch, "E1224", {"start": v(30.71, -49.75) * mm, "end": v(31.12, -50.01) * mm});
            skLineSegment(sketch, "E1225", {"start": v(31.12, -50.01) * mm, "end": v(31.55, -50.28) * mm});
            skLineSegment(sketch, "E1226", {"start": v(31.55, -50.28) * mm, "end": v(32, -50.55) * mm});
            skLineSegment(sketch, "E1227", {"start": v(32, -50.55) * mm, "end": v(32.48, -50.82) * mm});
            skLineSegment(sketch, "E1228", {"start": v(32.48, -50.82) * mm, "end": v(32.98, -51.09) * mm});
            skLineSegment(sketch, "E1229", {"start": v(32.98, -51.09) * mm, "end": v(33.5, -51.36) * mm});
            skLineSegment(sketch, "E1230", {"start": v(33.5, -51.36) * mm, "end": v(34.04, -51.62) * mm});
            skLineSegment(sketch, "E1231", {"start": v(34.04, -51.62) * mm, "end": v(34.6, -51.89) * mm});
            skLineSegment(sketch, "E1232", {"start": v(34.6, -51.89) * mm, "end": v(35.2, -52.15) * mm});
            skLineSegment(sketch, "E1233", {"start": v(35.2, -52.15) * mm, "end": v(35.81, -52.41) * mm});
            skLineSegment(sketch, "E1234", {"start": v(35.81, -52.41) * mm, "end": v(36.45, -52.67) * mm});
            skLineSegment(sketch, "E1235", {"start": v(36.45, -52.67) * mm, "end": v(37.11, -52.92) * mm});
            skLineSegment(sketch, "E1236", {"start": v(37.11, -52.92) * mm, "end": v(37.8, -53.16) * mm});
            skLineSegment(sketch, "E1237", {"start": v(37.8, -53.16) * mm, "end": v(38.5, -53.4) * mm});
            skLineSegment(sketch, "E1238", {"start": v(38.5, -53.4) * mm, "end": v(39.06, -53.38) * mm});
            skLineSegment(sketch, "E1239", {"start": v(39.06, -53.38) * mm, "end": v(40.75, -52.1) * mm});
            skLineSegment(sketch, "E1240", {"start": v(40.75, -52.1) * mm, "end": v(40.9, -51.57) * mm});
            skLineSegment(sketch, "E1241", {"start": v(40.9, -51.57) * mm, "end": v(40.87, -50.83) * mm});
            skLineSegment(sketch, "E1242", {"start": v(40.87, -50.83) * mm, "end": v(40.83, -50.1) * mm});
            skLineSegment(sketch, "E1243", {"start": v(40.83, -50.1) * mm, "end": v(40.77, -49.4) * mm});
            skLineSegment(sketch, "E1244", {"start": v(40.77, -49.4) * mm, "end": v(40.7, -48.72) * mm});
            skLineSegment(sketch, "E1245", {"start": v(40.7, -48.72) * mm, "end": v(40.61, -48.06) * mm});
            skLineSegment(sketch, "E1246", {"start": v(40.61, -48.06) * mm, "end": v(40.52, -47.42) * mm});
            skLineSegment(sketch, "E1247", {"start": v(40.52, -47.42) * mm, "end": v(40.42, -46.8) * mm});
            skLineSegment(sketch, "E1248", {"start": v(40.42, -46.8) * mm, "end": v(40.3, -46.2) * mm});
            skLineSegment(sketch, "E1249", {"start": v(40.3, -46.2) * mm, "end": v(40.2, -45.63) * mm});
            skLineSegment(sketch, "E1250", {"start": v(40.2, -45.63) * mm, "end": v(40.07, -45.08) * mm});
            skLineSegment(sketch, "E1251", {"start": v(40.07, -45.08) * mm, "end": v(39.94, -44.55) * mm});
            skLineSegment(sketch, "E1252", {"start": v(39.94, -44.55) * mm, "end": v(39.8, -44.04) * mm});
            skLineSegment(sketch, "E1253", {"start": v(39.8, -44.04) * mm, "end": v(39.66, -43.55) * mm});
            skLineSegment(sketch, "E1254", {"start": v(39.66, -43.55) * mm, "end": v(39.52, -43.08) * mm});
            skLineSegment(sketch, "E1255", {"start": v(39.52, -43.08) * mm, "end": v(39.37, -42.64) * mm});
            skLineSegment(sketch, "E1256", {"start": v(39.37, -42.64) * mm, "end": v(39.22, -42.22) * mm});
            skLineSegment(sketch, "E1257", {"start": v(39.22, -42.22) * mm, "end": v(39.08, -41.82) * mm});
            skLineSegment(sketch, "E1258", {"start": v(39.08, -41.82) * mm, "end": v(38.93, -41.44) * mm});
            skLineSegment(sketch, "E1259", {"start": v(38.93, -41.44) * mm, "end": v(38.78, -41.08) * mm});
            skLineSegment(sketch, "E1260", {"start": v(38.78, -41.08) * mm, "end": v(38.63, -40.75) * mm});
            skLineSegment(sketch, "E1261", {"start": v(38.63, -40.75) * mm, "end": v(38.48, -40.43) * mm});
            skLineSegment(sketch, "E1262", {"start": v(38.48, -40.43) * mm, "end": v(38.34, -40.14) * mm});
            skLineSegment(sketch, "E1263", {"start": v(38.34, -40.14) * mm, "end": v(38.2, -39.86) * mm});
            skLineSegment(sketch, "E1264", {"start": v(38.2, -39.86) * mm, "end": v(38.06, -39.61) * mm});
            skLineSegment(sketch, "E1265", {"start": v(38.06, -39.61) * mm, "end": v(37.93, -39.38) * mm});
            skLineSegment(sketch, "E1266", {"start": v(37.93, -39.38) * mm, "end": v(37.8, -39.17) * mm});
            skLineSegment(sketch, "E1267", {"start": v(37.8, -39.17) * mm, "end": v(37.69, -38.97) * mm});
            skLineSegment(sketch, "E1268", {"start": v(37.69, -38.97) * mm, "end": v(37.58, -38.8) * mm});
            skLineSegment(sketch, "E1269", {"start": v(37.58, -38.8) * mm, "end": v(37.47, -38.64) * mm});
            skLineSegment(sketch, "E1270", {"start": v(37.47, -38.64) * mm, "end": v(37.38, -38.5) * mm});
            skLineSegment(sketch, "E1271", {"start": v(37.38, -38.5) * mm, "end": v(37.3, -38.38) * mm});
            skLineSegment(sketch, "E1272", {"start": v(37.3, -38.38) * mm, "end": v(37.21, -38.28) * mm});
            skLineSegment(sketch, "E1273", {"start": v(37.21, -38.28) * mm, "end": v(37.15, -38.2) * mm});
            skLineSegment(sketch, "E1274", {"start": v(37.15, -38.2) * mm, "end": v(37.1, -38.13) * mm});
            skLineSegment(sketch, "E1275", {"start": v(37.1, -38.13) * mm, "end": v(37.05, -38.08) * mm});
            skLineSegment(sketch, "E1276", {"start": v(37.05, -38.08) * mm, "end": v(37.02, -38.04) * mm});
            skLineSegment(sketch, "E1277", {"start": v(37.02, -38.04) * mm, "end": v(37, -38.02) * mm});
            skLineSegment(sketch, "E1278", {"start": v(37, -38.02) * mm, "end": v(36.21, -37.21) * mm});
            skLineSegment(sketch, "E1279", {"start": v(36.21, -37.21) * mm, "end": v(39.78, -33.38) * mm});
            skLineSegment(sketch, "E1280", {"start": v(39.78, -33.38) * mm, "end": v(40.64, -34.1) * mm});
            skLineSegment(sketch, "E1281", {"start": v(40.64, -34.1) * mm, "end": v(40.66, -34.12) * mm});
            skLineSegment(sketch, "E1282", {"start": v(40.66, -34.12) * mm, "end": v(40.7, -34.15) * mm});
            skLineSegment(sketch, "E1283", {"start": v(40.7, -34.15) * mm, "end": v(40.75, -34.19) * mm});
            skLineSegment(sketch, "E1284", {"start": v(40.75, -34.19) * mm, "end": v(40.83, -34.24) * mm});
            skLineSegment(sketch, "E1285", {"start": v(40.83, -34.24) * mm, "end": v(40.92, -34.3) * mm});
            skLineSegment(sketch, "E1286", {"start": v(40.92, -34.3) * mm, "end": v(41.02, -34.37) * mm});
            skLineSegment(sketch, "E1287", {"start": v(41.02, -34.37) * mm, "end": v(41.15, -34.44) * mm});
            skLineSegment(sketch, "E1288", {"start": v(41.15, -34.44) * mm, "end": v(41.3, -34.53) * mm});
            skLineSegment(sketch, "E1289", {"start": v(41.3, -34.53) * mm, "end": v(41.46, -34.62) * mm});
            skLineSegment(sketch, "E1290", {"start": v(41.46, -34.62) * mm, "end": v(41.64, -34.72) * mm});
            skLineSegment(sketch, "E1291", {"start": v(41.64, -34.72) * mm, "end": v(41.84, -34.83) * mm});
            skLineSegment(sketch, "E1292", {"start": v(41.84, -34.83) * mm, "end": v(42.06, -34.93) * mm});
            skLineSegment(sketch, "E1293", {"start": v(42.06, -34.93) * mm, "end": v(42.3, -35.05) * mm});
            skLineSegment(sketch, "E1294", {"start": v(42.3, -35.05) * mm, "end": v(42.57, -35.16) * mm});
            skLineSegment(sketch, "E1295", {"start": v(42.57, -35.16) * mm, "end": v(42.85, -35.28) * mm});
            skLineSegment(sketch, "E1296", {"start": v(42.85, -35.28) * mm, "end": v(43.15, -35.4) * mm});
            skLineSegment(sketch, "E1297", {"start": v(43.15, -35.4) * mm, "end": v(43.48, -35.53) * mm});
            skLineSegment(sketch, "E1298", {"start": v(43.48, -35.53) * mm, "end": v(43.82, -35.65) * mm});
            skLineSegment(sketch, "E1299", {"start": v(43.82, -35.65) * mm, "end": v(44.2, -35.77) * mm});
            skLineSegment(sketch, "E1300", {"start": v(44.2, -35.77) * mm, "end": v(44.58, -35.9) * mm});
            skLineSegment(sketch, "E1301", {"start": v(44.58, -35.9) * mm, "end": v(44.99, -36.01) * mm});
            skLineSegment(sketch, "E1302", {"start": v(44.99, -36.01) * mm, "end": v(45.42, -36.13) * mm});
            skLineSegment(sketch, "E1303", {"start": v(45.42, -36.13) * mm, "end": v(45.87, -36.24) * mm});
            skLineSegment(sketch, "E1304", {"start": v(45.87, -36.24) * mm, "end": v(46.35, -36.35) * mm});
            skLineSegment(sketch, "E1305", {"start": v(46.35, -36.35) * mm, "end": v(46.84, -36.45) * mm});
            skLineSegment(sketch, "E1306", {"start": v(46.84, -36.45) * mm, "end": v(47.36, -36.55) * mm});
            skLineSegment(sketch, "E1307", {"start": v(47.36, -36.55) * mm, "end": v(47.9, -36.64) * mm});
            skLineSegment(sketch, "E1308", {"start": v(47.9, -36.64) * mm, "end": v(48.46, -36.73) * mm});
            skLineSegment(sketch, "E1309", {"start": v(48.46, -36.73) * mm, "end": v(49.04, -36.8) * mm});
            skLineSegment(sketch, "E1310", {"start": v(49.04, -36.8) * mm, "end": v(49.65, -36.87) * mm});
            skLineSegment(sketch, "E1311", {"start": v(49.65, -36.87) * mm, "end": v(50.27, -36.92) * mm});
            skLineSegment(sketch, "E1312", {"start": v(50.27, -36.92) * mm, "end": v(50.91, -36.97) * mm});
            skLineSegment(sketch, "E1313", {"start": v(50.91, -36.97) * mm, "end": v(51.58, -37) * mm});
            skLineSegment(sketch, "E1314", {"start": v(51.58, -37) * mm, "end": v(52.26, -37.02) * mm});
            skLineSegment(sketch, "E1315", {"start": v(52.26, -37.02) * mm, "end": v(52.97, -37.03) * mm});
            skLineSegment(sketch, "E1316", {"start": v(52.97, -37.03) * mm, "end": v(53.7, -37.03) * mm});
            skLineSegment(sketch, "E1317", {"start": v(53.7, -37.03) * mm, "end": v(54.44, -37) * mm});
            skLineSegment(sketch, "E1318", {"start": v(54.44, -37) * mm, "end": v(54.96, -36.8) * mm});
            skLineSegment(sketch, "E1319", {"start": v(54.96, -36.8) * mm, "end": v(56.11, -35.03) * mm});
            skLineSegment(sketch, "E1320", {"start": v(56.11, -35.03) * mm, "end": v(56.08, -34.47) * mm});
            skLineSegment(sketch, "E1321", {"start": v(56.08, -34.47) * mm, "end": v(55.8, -33.78) * mm});
            skLineSegment(sketch, "E1322", {"start": v(55.8, -33.78) * mm, "end": v(55.5, -33.12) * mm});
            skLineSegment(sketch, "E1323", {"start": v(55.5, -33.12) * mm, "end": v(55.2, -32.48) * mm});
            skLineSegment(sketch, "E1324", {"start": v(55.2, -32.48) * mm, "end": v(54.9, -31.86) * mm});
            skLineSegment(sketch, "E1325", {"start": v(54.9, -31.86) * mm, "end": v(54.6, -31.27) * mm});
            skLineSegment(sketch, "E1326", {"start": v(54.6, -31.27) * mm, "end": v(54.3, -30.7) * mm});
            skLineSegment(sketch, "E1327", {"start": v(54.3, -30.7) * mm, "end": v(53.99, -30.15) * mm});
            skLineSegment(sketch, "E1328", {"start": v(53.99, -30.15) * mm, "end": v(53.68, -29.63) * mm});
            skLineSegment(sketch, "E1329", {"start": v(53.68, -29.63) * mm, "end": v(53.37, -29.13) * mm});
            skLineSegment(sketch, "E1330", {"start": v(53.37, -29.13) * mm, "end": v(53.07, -28.65) * mm});
            skLineSegment(sketch, "E1331", {"start": v(53.07, -28.65) * mm, "end": v(52.76, -28.2) * mm});
            skLineSegment(sketch, "E1332", {"start": v(52.76, -28.2) * mm, "end": v(52.46, -27.77) * mm});
            skLineSegment(sketch, "E1333", {"start": v(52.46, -27.77) * mm, "end": v(52.16, -27.36) * mm});
            skLineSegment(sketch, "E1334", {"start": v(52.16, -27.36) * mm, "end": v(51.87, -26.97) * mm});
            skLineSegment(sketch, "E1335", {"start": v(51.87, -26.97) * mm, "end": v(51.58, -26.6) * mm});
            skLineSegment(sketch, "E1336", {"start": v(51.58, -26.6) * mm, "end": v(51.3, -26.26) * mm});
            skLineSegment(sketch, "E1337", {"start": v(51.3, -26.26) * mm, "end": v(51.02, -25.93) * mm});
            skLineSegment(sketch, "E1338", {"start": v(51.02, -25.93) * mm, "end": v(50.75, -25.63) * mm});
            skLineSegment(sketch, "E1339", {"start": v(50.75, -25.63) * mm, "end": v(50.49, -25.34) * mm});
            skLineSegment(sketch, "E1340", {"start": v(50.49, -25.34) * mm, "end": v(50.24, -25.08) * mm});
            skLineSegment(sketch, "E1341", {"start": v(50.24, -25.08) * mm, "end": v(50, -24.83) * mm});
            skLineSegment(sketch, "E1342", {"start": v(50, -24.83) * mm, "end": v(49.76, -24.6) * mm});
            skLineSegment(sketch, "E1343", {"start": v(49.76, -24.6) * mm, "end": v(49.53, -24.4) * mm});
            skLineSegment(sketch, "E1344", {"start": v(49.53, -24.4) * mm, "end": v(49.32, -24.2) * mm});
            skLineSegment(sketch, "E1345", {"start": v(49.32, -24.2) * mm, "end": v(49.11, -24.03) * mm});
            skLineSegment(sketch, "E1346", {"start": v(49.11, -24.03) * mm, "end": v(48.92, -23.87) * mm});
            skLineSegment(sketch, "E1347", {"start": v(48.92, -23.87) * mm, "end": v(48.75, -23.73) * mm});
            skLineSegment(sketch, "E1348", {"start": v(48.75, -23.73) * mm, "end": v(48.58, -23.6) * mm});
            skLineSegment(sketch, "E1349", {"start": v(48.58, -23.6) * mm, "end": v(48.43, -23.5) * mm});
            skLineSegment(sketch, "E1350", {"start": v(48.43, -23.5) * mm, "end": v(48.3, -23.4) * mm});
            skLineSegment(sketch, "E1351", {"start": v(48.3, -23.4) * mm, "end": v(48.17, -23.32) * mm});
            skLineSegment(sketch, "E1352", {"start": v(48.17, -23.32) * mm, "end": v(48.06, -23.25) * mm});
            skLineSegment(sketch, "E1353", {"start": v(48.06, -23.25) * mm, "end": v(47.97, -23.19) * mm});
            skLineSegment(sketch, "E1354", {"start": v(47.97, -23.19) * mm, "end": v(47.9, -23.14) * mm});
            skLineSegment(sketch, "E1355", {"start": v(47.9, -23.14) * mm, "end": v(47.84, -23.1) * mm});
            skLineSegment(sketch, "E1356", {"start": v(47.84, -23.1) * mm, "end": v(47.8, -23.09) * mm});
            skLineSegment(sketch, "E1357", {"start": v(47.8, -23.09) * mm, "end": v(47.77, -23.08) * mm});
            skLineSegment(sketch, "E1358", {"start": v(47.77, -23.08) * mm, "end": v(46.76, -22.58) * mm});
            skLineSegment(sketch, "E1359", {"start": v(46.76, -22.58) * mm, "end": v(48.8, -17.76) * mm});
            skLineSegment(sketch, "E1360", {"start": v(48.8, -17.76) * mm, "end": v(49.85, -18.14) * mm});
            skLineSegment(sketch, "E1361", {"start": v(49.85, -18.14) * mm, "end": v(49.88, -18.15) * mm});
            skLineSegment(sketch, "E1362", {"start": v(49.88, -18.15) * mm, "end": v(49.92, -18.17) * mm});
            skLineSegment(sketch, "E1363", {"start": v(49.92, -18.17) * mm, "end": v(49.99, -18.19) * mm});
            skLineSegment(sketch, "E1364", {"start": v(49.99, -18.19) * mm, "end": v(50.07, -18.2) * mm});
            skLineSegment(sketch, "E1365", {"start": v(50.07, -18.2) * mm, "end": v(50.18, -18.24) * mm});
            skLineSegment(sketch, "E1366", {"start": v(50.18, -18.24) * mm, "end": v(50.3, -18.26) * mm});
            skLineSegment(sketch, "E1367", {"start": v(50.3, -18.26) * mm, "end": v(50.45, -18.3) * mm});
            skLineSegment(sketch, "E1368", {"start": v(50.45, -18.3) * mm, "end": v(50.61, -18.33) * mm});
            skLineSegment(sketch, "E1369", {"start": v(50.61, -18.33) * mm, "end": v(50.8, -18.36) * mm});
            skLineSegment(sketch, "E1370", {"start": v(50.8, -18.36) * mm, "end": v(51, -18.39) * mm});
            skLineSegment(sketch, "E1371", {"start": v(51, -18.39) * mm, "end": v(51.23, -18.41) * mm});
            skLineSegment(sketch, "E1372", {"start": v(51.23, -18.41) * mm, "end": v(51.47, -18.44) * mm});
            skLineSegment(sketch, "E1373", {"start": v(51.47, -18.44) * mm, "end": v(51.74, -18.47) * mm});
            skLineSegment(sketch, "E1374", {"start": v(51.74, -18.47) * mm, "end": v(52.03, -18.49) * mm});
            skLineSegment(sketch, "E1375", {"start": v(52.03, -18.49) * mm, "end": v(52.33, -18.5) * mm});
            skLineSegment(sketch, "E1376", {"start": v(52.33, -18.5) * mm, "end": v(52.66, -18.51) * mm});
            skLineSegment(sketch, "E1377", {"start": v(52.66, -18.51) * mm, "end": v(53, -18.52) * mm});
            skLineSegment(sketch, "E1378", {"start": v(53, -18.52) * mm, "end": v(53.37, -18.51) * mm});
            skLineSegment(sketch, "E1379", {"start": v(53.37, -18.51) * mm, "end": v(53.76, -18.5) * mm});
            skLineSegment(sketch, "E1380", {"start": v(53.76, -18.5) * mm, "end": v(54.17, -18.48) * mm});
            skLineSegment(sketch, "E1381", {"start": v(54.17, -18.48) * mm, "end": v(54.6, -18.45) * mm});
            skLineSegment(sketch, "E1382", {"start": v(54.6, -18.45) * mm, "end": v(55.04, -18.42) * mm});
            skLineSegment(sketch, "E1383", {"start": v(55.04, -18.42) * mm, "end": v(55.5, -18.37) * mm});
            skLineSegment(sketch, "E1384", {"start": v(55.5, -18.37) * mm, "end": v(55.99, -18.3) * mm});
            skLineSegment(sketch, "E1385", {"start": v(55.99, -18.3) * mm, "end": v(56.49, -18.24) * mm});
            skLineSegment(sketch, "E1386", {"start": v(56.49, -18.24) * mm, "end": v(57, -18.15) * mm});
            skLineSegment(sketch, "E1387", {"start": v(57, -18.15) * mm, "end": v(57.54, -18.05) * mm});
            skLineSegment(sketch, "E1388", {"start": v(57.54, -18.05) * mm, "end": v(58.1, -17.94) * mm});
            skLineSegment(sketch, "E1389", {"start": v(58.1, -17.94) * mm, "end": v(58.67, -17.8) * mm});
            skLineSegment(sketch, "E1390", {"start": v(58.67, -17.8) * mm, "end": v(59.26, -17.66) * mm});
            skLineSegment(sketch, "E1391", {"start": v(59.26, -17.66) * mm, "end": v(59.87, -17.5) * mm});
            skLineSegment(sketch, "E1392", {"start": v(59.87, -17.5) * mm, "end": v(60.49, -17.32) * mm});
            skLineSegment(sketch, "E1393", {"start": v(60.49, -17.32) * mm, "end": v(61.12, -17.13) * mm});
            skLineSegment(sketch, "E1394", {"start": v(61.12, -17.13) * mm, "end": v(61.78, -16.91) * mm});
            skLineSegment(sketch, "E1395", {"start": v(61.78, -16.91) * mm, "end": v(62.44, -16.68) * mm});
            skLineSegment(sketch, "E1396", {"start": v(62.44, -16.68) * mm, "end": v(63.12, -16.43) * mm});
            skLineSegment(sketch, "E1397", {"start": v(63.12, -16.43) * mm, "end": v(63.82, -16.15) * mm});
            skLineSegment(sketch, "E1398", {"start": v(63.82, -16.15) * mm, "end": v(64.23, -15.79) * mm});
            skLineSegment(sketch, "E1399", {"start": v(64.23, -15.79) * mm, "end": v(64.7, -13.72) * mm});
            skLineSegment(sketch, "E1400", {"start": v(64.7, -13.72) * mm, "end": v(64.49, -13.21) * mm});
            skLineSegment(sketch, "E1401", {"start": v(64.49, -13.21) * mm, "end": v(63.98, -12.66) * mm});
            skLineSegment(sketch, "E1402", {"start": v(63.98, -12.66) * mm, "end": v(63.48, -12.14) * mm});
            skLineSegment(sketch, "E1403", {"start": v(63.48, -12.14) * mm, "end": v(62.98, -11.64) * mm});
            skLineSegment(sketch, "E1404", {"start": v(62.98, -11.64) * mm, "end": v(62.49, -11.16) * mm});
            skLineSegment(sketch, "E1405", {"start": v(62.49, -11.16) * mm, "end": v(62, -10.7) * mm});
            skLineSegment(sketch, "E1406", {"start": v(62, -10.7) * mm, "end": v(61.52, -10.28) * mm});
            skLineSegment(sketch, "E1407", {"start": v(61.52, -10.28) * mm, "end": v(61.04, -9.87) * mm});
            skLineSegment(sketch, "E1408", {"start": v(61.04, -9.87) * mm, "end": v(60.58, -9.48) * mm});
            skLineSegment(sketch, "E1409", {"start": v(60.58, -9.48) * mm, "end": v(60.12, -9.12) * mm});
            skLineSegment(sketch, "E1410", {"start": v(60.12, -9.12) * mm, "end": v(59.67, -8.78) * mm});
            skLineSegment(sketch, "E1411", {"start": v(59.67, -8.78) * mm, "end": v(59.23, -8.45) * mm});
            skLineSegment(sketch, "E1412", {"start": v(59.23, -8.45) * mm, "end": v(58.8, -8.15) * mm});
            skLineSegment(sketch, "E1413", {"start": v(58.8, -8.15) * mm, "end": v(58.38, -7.87) * mm});
            skLineSegment(sketch, "E1414", {"start": v(58.38, -7.87) * mm, "end": v(57.97, -7.6) * mm});
            skLineSegment(sketch, "E1415", {"start": v(57.97, -7.6) * mm, "end": v(57.57, -7.36) * mm});
            skLineSegment(sketch, "E1416", {"start": v(57.57, -7.36) * mm, "end": v(57.19, -7.13) * mm});
            skLineSegment(sketch, "E1417", {"start": v(57.19, -7.13) * mm, "end": v(56.81, -6.92) * mm});
            skLineSegment(sketch, "E1418", {"start": v(56.81, -6.92) * mm, "end": v(56.46, -6.72) * mm});
            skLineSegment(sketch, "E1419", {"start": v(56.46, -6.72) * mm, "end": v(56.11, -6.55) * mm});
            skLineSegment(sketch, "E1420", {"start": v(56.11, -6.55) * mm, "end": v(55.78, -6.38) * mm});
            skLineSegment(sketch, "E1421", {"start": v(55.78, -6.38) * mm, "end": v(55.47, -6.24) * mm});
            skLineSegment(sketch, "E1422", {"start": v(55.47, -6.24) * mm, "end": v(55.17, -6.1) * mm});
            skLineSegment(sketch, "E1423", {"start": v(55.17, -6.1) * mm, "end": v(54.89, -5.98) * mm});
            skLineSegment(sketch, "E1424", {"start": v(54.89, -5.98) * mm, "end": v(54.62, -5.88) * mm});
            skLineSegment(sketch, "E1425", {"start": v(54.62, -5.88) * mm, "end": v(54.37, -5.78) * mm});
            skLineSegment(sketch, "E1426", {"start": v(54.37, -5.78) * mm, "end": v(54.14, -5.7) * mm});
            skLineSegment(sketch, "E1427", {"start": v(54.14, -5.7) * mm, "end": v(53.92, -5.63) * mm});
            skLineSegment(sketch, "E1428", {"start": v(53.92, -5.63) * mm, "end": v(53.72, -5.57) * mm});
            skLineSegment(sketch, "E1429", {"start": v(53.72, -5.57) * mm, "end": v(53.54, -5.51) * mm});
            skLineSegment(sketch, "E1430", {"start": v(53.54, -5.51) * mm, "end": v(53.38, -5.47) * mm});
            skLineSegment(sketch, "E1431", {"start": v(53.38, -5.47) * mm, "end": v(53.24, -5.43) * mm});
            skLineSegment(sketch, "E1432", {"start": v(53.24, -5.43) * mm, "end": v(53.12, -5.4) * mm});
            skLineSegment(sketch, "E1433", {"start": v(53.12, -5.4) * mm, "end": v(53, -5.38) * mm});
            skLineSegment(sketch, "E1434", {"start": v(53, -5.38) * mm, "end": v(52.92, -5.37) * mm});
            skLineSegment(sketch, "E1435", {"start": v(52.92, -5.37) * mm, "end": v(52.86, -5.36) * mm});
            skLineSegment(sketch, "E1436", {"start": v(52.86, -5.36) * mm, "end": v(52.8, -5.35) * mm});
            skLineSegment(sketch, "E1437", {"start": v(52.8, -5.35) * mm, "end": v(52.78, -5.35) * mm});
            skLineSegment(sketch, "E1438", {"start": v(52.78, -5.35) * mm, "end": v(51.66, -5.23) * mm});
            skLineSegment(sketch, "E1439", {"start": v(51.66, -5.23) * mm, "end": v(51.92, 0) * mm});
            skCircle(sketch, "E1440", {"center": v(0, 0) * mm, "radius": 3.84 * mm});
            skLineSegment(sketch, "E1441", {"start": v(73.46, 66.1) * mm, "end": v(73.46, -66.1) * mm});
            skSolve(sketch);
        }
        {
            var Q0;
            Q0=makeQuery(id+"F0.imprint","IMPRINT",FACE,{"disambiguationData":[TD([[makeQuery(id+"F0.imprint","IMPRINT",EDGE,{"derivedFrom":sQuery(id+"F0.wireOp",EDGE,"E0")}),1.0]])]});
            extrude(context, id + "F1", {"entities" : qUnion([Q0]), "depth" : 1 / 406.4 * mm, "offsetDistance" : 25.4 * mm});
        }
    });
